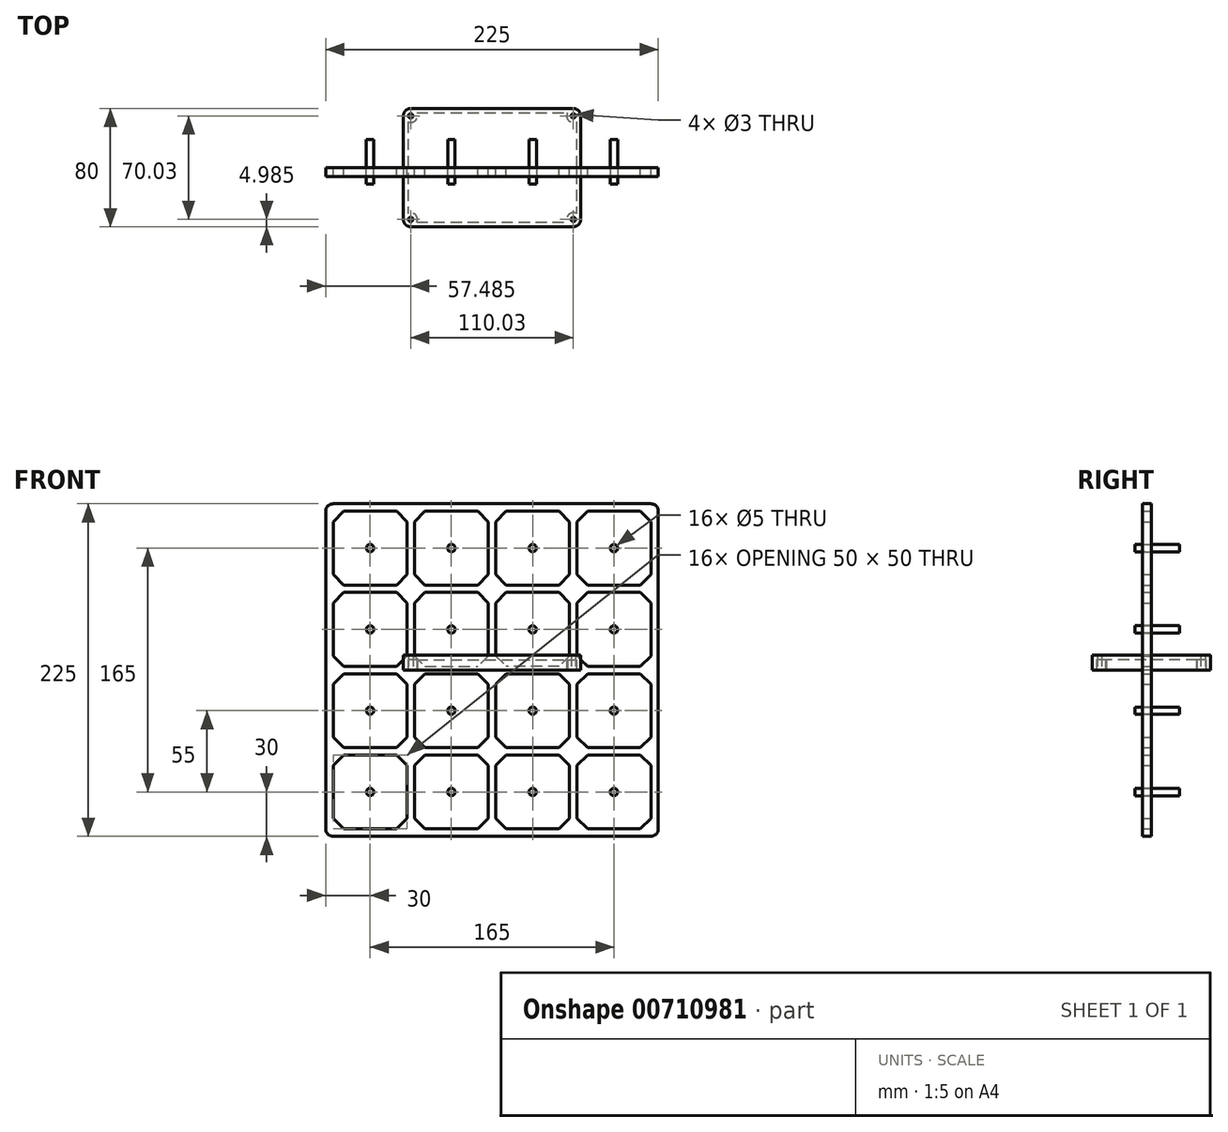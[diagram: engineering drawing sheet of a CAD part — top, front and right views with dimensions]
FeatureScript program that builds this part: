
annotation { "Feature Type Name" : "Feature", "Feature Type Description" : "" }
export const myFeature = defineFeature(function(context is Context, id is Id, definition is map)
    precondition{}
    {
        {
            var Q0;
            Q0=qCreatedBy(makeId("Front.planeOp"),FACE);
            var sketch = newSketch(context, id + "F0", { "sketchPlane" : qUnion([Q0])});
            skLineSegment(sketch, "E0.bottom", {"start": v(-112.5, 112.5) * mm, "end": v(112.5, 112.5) * mm});
            skLineSegment(sketch, "E0.top", {"start": v(-112.5, -112.5) * mm, "end": v(112.5, -112.5) * mm});
            skLineSegment(sketch, "E0.left", {"start": v(-112.5, 112.5) * mm, "end": v(-112.5, -112.5) * mm});
            skLineSegment(sketch, "E0.right", {"start": v(112.5, 112.5) * mm, "end": v(112.5, -112.5) * mm});
            skLineSegment(sketch, "E1", {"start": v(-107.5, 82.5) * mm, "end": v(-57.5, 82.5) * mm, "construction": true});
            skLineSegment(sketch, "E2", {"start": v(-82.5, 107.5) * mm, "end": v(-82.5, 57.5) * mm, "construction": true});
            skPoint(sketch, "E3", {"position": v(-82.5, 82.5) * mm});
            skLineSegment(sketch, "E4", {"start": v(-107.5, 82.5) * mm, "end": v(-107.5, 100.43) * mm});
            skLineSegment(sketch, "E5", {"start": v(-107.5, 100.43) * mm, "end": v(-100.43, 107.5) * mm});
            skLineSegment(sketch, "E6", {"start": v(-100.43, 107.5) * mm, "end": v(-82.5, 107.5) * mm});
            skLineSegment(sketch, "E7.MirrorCS", {"start": v(-57.5, 82.5) * mm, "end": v(-57.5, 100.43) * mm});
            skLineSegment(sketch, "E8.MirrorCS", {"start": v(-64.57, 107.5) * mm, "end": v(-82.5, 107.5) * mm});
            skLineSegment(sketch, "E9.MirrorCS", {"start": v(-57.5, 100.43) * mm, "end": v(-64.57, 107.5) * mm});
            skLineSegment(sketch, "E10.MirrorCS", {"start": v(-57.5, 82.5) * mm, "end": v(-107.5, 82.5) * mm, "construction": true});
            skLineSegment(sketch, "E11.MirrorCS", {"start": v(-57.5, 82.5) * mm, "end": v(-57.5, 64.57) * mm});
            skLineSegment(sketch, "E12.MirrorCS", {"start": v(-57.5, 64.57) * mm, "end": v(-64.57, 57.5) * mm});
            skLineSegment(sketch, "E13.MirrorCS", {"start": v(-64.57, 57.5) * mm, "end": v(-82.5, 57.5) * mm});
            skLineSegment(sketch, "E14.MirrorCS", {"start": v(-100.43, 57.5) * mm, "end": v(-82.5, 57.5) * mm});
            skLineSegment(sketch, "E15.MirrorCS", {"start": v(-107.5, 82.5) * mm, "end": v(-107.5, 64.57) * mm});
            skLineSegment(sketch, "E16.MirrorCS", {"start": v(-107.5, 64.57) * mm, "end": v(-100.43, 57.5) * mm});
            skLineSegment(sketch, "E17.0.1.0", {"start": v(-107.5, 45.43) * mm, "end": v(-100.43, 52.5) * mm});
            skPoint(sketch, "E17.0.1.1", {"position": v(-82.5, 27.5) * mm});
            skLineSegment(sketch, "E17.0.1.2", {"start": v(-57.5, 27.5) * mm, "end": v(-57.5, 9.57) * mm});
            skLineSegment(sketch, "E17.0.1.3", {"start": v(-57.5, 45.43) * mm, "end": v(-64.57, 52.5) * mm});
            skLineSegment(sketch, "E17.0.1.4", {"start": v(-57.5, 27.5) * mm, "end": v(-57.5, 45.43) * mm});
            skLineSegment(sketch, "E17.0.1.5", {"start": v(-57.5, 9.57) * mm, "end": v(-64.57, 2.5) * mm});
            skLineSegment(sketch, "E17.0.1.6", {"start": v(-107.5, 27.5) * mm, "end": v(-107.5, 45.43) * mm});
            skLineSegment(sketch, "E17.0.1.7", {"start": v(-64.57, 2.5) * mm, "end": v(-82.5, 2.5) * mm});
            skLineSegment(sketch, "E17.0.1.8", {"start": v(-82.5, 52.5) * mm, "end": v(-82.5, 2.5) * mm, "construction": true});
            skLineSegment(sketch, "E17.0.1.9", {"start": v(-57.5, 27.5) * mm, "end": v(-107.5, 27.5) * mm, "construction": true});
            skLineSegment(sketch, "E17.0.1.10", {"start": v(-107.5, 27.5) * mm, "end": v(-107.5, 9.57) * mm});
            skLineSegment(sketch, "E17.0.1.11", {"start": v(-107.5, 9.57) * mm, "end": v(-100.43, 2.5) * mm});
            skLineSegment(sketch, "E17.0.1.12", {"start": v(-64.57, 52.5) * mm, "end": v(-82.5, 52.5) * mm});
            skLineSegment(sketch, "E17.0.1.13", {"start": v(-100.43, 52.5) * mm, "end": v(-82.5, 52.5) * mm});
            skLineSegment(sketch, "E17.0.1.14", {"start": v(-100.43, 2.5) * mm, "end": v(-82.5, 2.5) * mm});
            skLineSegment(sketch, "E17.0.1.15", {"start": v(-107.5, 45.43) * mm, "end": v(-100.43, 52.5) * mm});
            skLineSegment(sketch, "E17.0.1.16", {"start": v(-107.5, 27.5) * mm, "end": v(-107.5, 45.43) * mm});
            skLineSegment(sketch, "E17.0.1.17", {"start": v(-57.5, 27.5) * mm, "end": v(-107.5, 27.5) * mm, "construction": true});
            skLineSegment(sketch, "E17.0.1.18", {"start": v(-57.5, 45.43) * mm, "end": v(-64.57, 52.5) * mm});
            skPoint(sketch, "E17.0.1.19", {"position": v(-82.5, 27.5) * mm});
            skLineSegment(sketch, "E17.0.1.20", {"start": v(-100.43, 52.5) * mm, "end": v(-82.5, 52.5) * mm});
            skLineSegment(sketch, "E17.0.1.21", {"start": v(-57.5, 27.5) * mm, "end": v(-57.5, 45.43) * mm});
            skLineSegment(sketch, "E17.0.1.22", {"start": v(-64.57, 52.5) * mm, "end": v(-82.5, 52.5) * mm});
            skLineSegment(sketch, "E17.0.1.23", {"start": v(-107.5, 27.5) * mm, "end": v(-57.5, 27.5) * mm, "construction": true});
            skLineSegment(sketch, "E17.0.1.24", {"start": v(-57.5, 45.43) * mm, "end": v(-64.57, 52.5) * mm});
            skLineSegment(sketch, "E17.0.1.25", {"start": v(-107.5, 45.43) * mm, "end": v(-100.43, 52.5) * mm});
            skLineSegment(sketch, "E17.0.1.26", {"start": v(-64.57, 52.5) * mm, "end": v(-82.5, 52.5) * mm});
            skLineSegment(sketch, "E17.0.1.27", {"start": v(-100.43, 52.5) * mm, "end": v(-82.5, 52.5) * mm});
            skLineSegment(sketch, "E17.0.1.28", {"start": v(-100.43, 52.5) * mm, "end": v(-82.5, 52.5) * mm});
            skLineSegment(sketch, "E17.0.1.29", {"start": v(-64.57, 52.5) * mm, "end": v(-82.5, 52.5) * mm});
            skLineSegment(sketch, "E17.0.1.30", {"start": v(-107.5, 27.5) * mm, "end": v(-57.5, 27.5) * mm, "construction": true});
            skLineSegment(sketch, "E17.0.2.0", {"start": v(-107.5, -9.57) * mm, "end": v(-100.43, -2.5) * mm});
            skPoint(sketch, "E17.0.2.1", {"position": v(-82.5, -27.5) * mm});
            skLineSegment(sketch, "E17.0.2.2", {"start": v(-57.5, -27.5) * mm, "end": v(-57.5, -45.43) * mm});
            skLineSegment(sketch, "E17.0.2.3", {"start": v(-57.5, -9.57) * mm, "end": v(-64.57, -2.5) * mm});
            skLineSegment(sketch, "E17.0.2.4", {"start": v(-57.5, -27.5) * mm, "end": v(-57.5, -9.57) * mm});
            skLineSegment(sketch, "E17.0.2.5", {"start": v(-57.5, -45.43) * mm, "end": v(-64.57, -52.5) * mm});
            skLineSegment(sketch, "E17.0.2.6", {"start": v(-107.5, -27.5) * mm, "end": v(-107.5, -9.57) * mm});
            skLineSegment(sketch, "E17.0.2.7", {"start": v(-64.57, -52.5) * mm, "end": v(-82.5, -52.5) * mm});
            skLineSegment(sketch, "E17.0.2.8", {"start": v(-82.5, -2.5) * mm, "end": v(-82.5, -52.5) * mm, "construction": true});
            skLineSegment(sketch, "E17.0.2.9", {"start": v(-57.5, -27.5) * mm, "end": v(-107.5, -27.5) * mm, "construction": true});
            skLineSegment(sketch, "E17.0.2.10", {"start": v(-107.5, -27.5) * mm, "end": v(-107.5, -45.43) * mm});
            skLineSegment(sketch, "E17.0.2.11", {"start": v(-107.5, -45.43) * mm, "end": v(-100.43, -52.5) * mm});
            skLineSegment(sketch, "E17.0.2.12", {"start": v(-64.57, -2.5) * mm, "end": v(-82.5, -2.5) * mm});
            skLineSegment(sketch, "E17.0.2.13", {"start": v(-100.43, -2.5) * mm, "end": v(-82.5, -2.5) * mm});
            skLineSegment(sketch, "E17.0.2.14", {"start": v(-100.43, -52.5) * mm, "end": v(-82.5, -52.5) * mm});
            skLineSegment(sketch, "E17.0.2.15", {"start": v(-107.5, -9.57) * mm, "end": v(-100.43, -2.5) * mm});
            skLineSegment(sketch, "E17.0.2.16", {"start": v(-107.5, -27.5) * mm, "end": v(-107.5, -9.57) * mm});
            skLineSegment(sketch, "E17.0.2.17", {"start": v(-57.5, -27.5) * mm, "end": v(-107.5, -27.5) * mm, "construction": true});
            skLineSegment(sketch, "E17.0.2.18", {"start": v(-57.5, -9.57) * mm, "end": v(-64.57, -2.5) * mm});
            skPoint(sketch, "E17.0.2.19", {"position": v(-82.5, -27.5) * mm});
            skLineSegment(sketch, "E17.0.2.20", {"start": v(-100.43, -2.5) * mm, "end": v(-82.5, -2.5) * mm});
            skLineSegment(sketch, "E17.0.2.21", {"start": v(-57.5, -27.5) * mm, "end": v(-57.5, -9.57) * mm});
            skLineSegment(sketch, "E17.0.2.22", {"start": v(-64.57, -2.5) * mm, "end": v(-82.5, -2.5) * mm});
            skLineSegment(sketch, "E17.0.2.23", {"start": v(-107.5, -27.5) * mm, "end": v(-57.5, -27.5) * mm, "construction": true});
            skLineSegment(sketch, "E17.0.2.24", {"start": v(-57.5, -9.57) * mm, "end": v(-64.57, -2.5) * mm});
            skLineSegment(sketch, "E17.0.2.25", {"start": v(-107.5, -9.57) * mm, "end": v(-100.43, -2.5) * mm});
            skLineSegment(sketch, "E17.0.2.26", {"start": v(-64.57, -2.5) * mm, "end": v(-82.5, -2.5) * mm});
            skLineSegment(sketch, "E17.0.2.27", {"start": v(-100.43, -2.5) * mm, "end": v(-82.5, -2.5) * mm});
            skLineSegment(sketch, "E17.0.2.28", {"start": v(-100.43, -2.5) * mm, "end": v(-82.5, -2.5) * mm});
            skLineSegment(sketch, "E17.0.2.29", {"start": v(-64.57, -2.5) * mm, "end": v(-82.5, -2.5) * mm});
            skLineSegment(sketch, "E17.0.2.30", {"start": v(-107.5, -27.5) * mm, "end": v(-57.5, -27.5) * mm, "construction": true});
            skLineSegment(sketch, "E17.0.3.0", {"start": v(-107.5, -64.57) * mm, "end": v(-100.43, -57.5) * mm});
            skPoint(sketch, "E17.0.3.1", {"position": v(-82.5, -82.5) * mm});
            skLineSegment(sketch, "E17.0.3.2", {"start": v(-57.5, -82.5) * mm, "end": v(-57.5, -100.43) * mm});
            skLineSegment(sketch, "E17.0.3.3", {"start": v(-57.5, -64.57) * mm, "end": v(-64.57, -57.5) * mm});
            skLineSegment(sketch, "E17.0.3.4", {"start": v(-57.5, -82.5) * mm, "end": v(-57.5, -64.57) * mm});
            skLineSegment(sketch, "E17.0.3.5", {"start": v(-57.5, -100.43) * mm, "end": v(-64.57, -107.5) * mm});
            skLineSegment(sketch, "E17.0.3.6", {"start": v(-107.5, -82.5) * mm, "end": v(-107.5, -64.57) * mm});
            skLineSegment(sketch, "E17.0.3.7", {"start": v(-64.57, -107.5) * mm, "end": v(-82.5, -107.5) * mm});
            skLineSegment(sketch, "E17.0.3.8", {"start": v(-82.5, -57.5) * mm, "end": v(-82.5, -107.5) * mm, "construction": true});
            skLineSegment(sketch, "E17.0.3.9", {"start": v(-57.5, -82.5) * mm, "end": v(-107.5, -82.5) * mm, "construction": true});
            skLineSegment(sketch, "E17.0.3.10", {"start": v(-107.5, -82.5) * mm, "end": v(-107.5, -100.43) * mm});
            skLineSegment(sketch, "E17.0.3.11", {"start": v(-107.5, -100.43) * mm, "end": v(-100.43, -107.5) * mm});
            skLineSegment(sketch, "E17.0.3.12", {"start": v(-64.57, -57.5) * mm, "end": v(-82.5, -57.5) * mm});
            skLineSegment(sketch, "E17.0.3.13", {"start": v(-100.43, -57.5) * mm, "end": v(-82.5, -57.5) * mm});
            skLineSegment(sketch, "E17.0.3.14", {"start": v(-100.43, -107.5) * mm, "end": v(-82.5, -107.5) * mm});
            skLineSegment(sketch, "E17.0.3.15", {"start": v(-107.5, -64.57) * mm, "end": v(-100.43, -57.5) * mm});
            skLineSegment(sketch, "E17.0.3.16", {"start": v(-107.5, -82.5) * mm, "end": v(-107.5, -64.57) * mm});
            skLineSegment(sketch, "E17.0.3.17", {"start": v(-57.5, -82.5) * mm, "end": v(-107.5, -82.5) * mm, "construction": true});
            skLineSegment(sketch, "E17.0.3.18", {"start": v(-57.5, -64.57) * mm, "end": v(-64.57, -57.5) * mm});
            skPoint(sketch, "E17.0.3.19", {"position": v(-82.5, -82.5) * mm});
            skLineSegment(sketch, "E17.0.3.20", {"start": v(-100.43, -57.5) * mm, "end": v(-82.5, -57.5) * mm});
            skLineSegment(sketch, "E17.0.3.21", {"start": v(-57.5, -82.5) * mm, "end": v(-57.5, -64.57) * mm});
            skLineSegment(sketch, "E17.0.3.22", {"start": v(-64.57, -57.5) * mm, "end": v(-82.5, -57.5) * mm});
            skLineSegment(sketch, "E17.0.3.23", {"start": v(-107.5, -82.5) * mm, "end": v(-57.5, -82.5) * mm, "construction": true});
            skLineSegment(sketch, "E17.0.3.24", {"start": v(-57.5, -64.57) * mm, "end": v(-64.57, -57.5) * mm});
            skLineSegment(sketch, "E17.0.3.25", {"start": v(-107.5, -64.57) * mm, "end": v(-100.43, -57.5) * mm});
            skLineSegment(sketch, "E17.0.3.26", {"start": v(-64.57, -57.5) * mm, "end": v(-82.5, -57.5) * mm});
            skLineSegment(sketch, "E17.0.3.27", {"start": v(-100.43, -57.5) * mm, "end": v(-82.5, -57.5) * mm});
            skLineSegment(sketch, "E17.0.3.28", {"start": v(-100.43, -57.5) * mm, "end": v(-82.5, -57.5) * mm});
            skLineSegment(sketch, "E17.0.3.29", {"start": v(-64.57, -57.5) * mm, "end": v(-82.5, -57.5) * mm});
            skLineSegment(sketch, "E17.0.3.30", {"start": v(-107.5, -82.5) * mm, "end": v(-57.5, -82.5) * mm, "construction": true});
            skLineSegment(sketch, "E17.1.0.0", {"start": v(-52.5, 100.43) * mm, "end": v(-45.43, 107.5) * mm});
            skPoint(sketch, "E17.1.0.1", {"position": v(-27.5, 82.5) * mm});
            skLineSegment(sketch, "E17.1.0.2", {"start": v(-2.5, 82.5) * mm, "end": v(-2.5, 64.57) * mm});
            skLineSegment(sketch, "E17.1.0.3", {"start": v(-2.5, 100.43) * mm, "end": v(-9.57, 107.5) * mm});
            skLineSegment(sketch, "E17.1.0.4", {"start": v(-2.5, 82.5) * mm, "end": v(-2.5, 100.43) * mm});
            skLineSegment(sketch, "E17.1.0.5", {"start": v(-2.5, 64.57) * mm, "end": v(-9.57, 57.5) * mm});
            skLineSegment(sketch, "E17.1.0.6", {"start": v(-52.5, 82.5) * mm, "end": v(-52.5, 100.43) * mm});
            skLineSegment(sketch, "E17.1.0.7", {"start": v(-9.57, 57.5) * mm, "end": v(-27.5, 57.5) * mm});
            skLineSegment(sketch, "E17.1.0.8", {"start": v(-27.5, 107.5) * mm, "end": v(-27.5, 57.5) * mm, "construction": true});
            skLineSegment(sketch, "E17.1.0.9", {"start": v(-2.5, 82.5) * mm, "end": v(-52.5, 82.5) * mm, "construction": true});
            skLineSegment(sketch, "E17.1.0.10", {"start": v(-52.5, 82.5) * mm, "end": v(-52.5, 64.57) * mm});
            skLineSegment(sketch, "E17.1.0.11", {"start": v(-52.5, 64.57) * mm, "end": v(-45.43, 57.5) * mm});
            skLineSegment(sketch, "E17.1.0.12", {"start": v(-9.57, 107.5) * mm, "end": v(-27.5, 107.5) * mm});
            skLineSegment(sketch, "E17.1.0.13", {"start": v(-45.43, 107.5) * mm, "end": v(-27.5, 107.5) * mm});
            skLineSegment(sketch, "E17.1.0.14", {"start": v(-45.43, 57.5) * mm, "end": v(-27.5, 57.5) * mm});
            skLineSegment(sketch, "E17.1.0.15", {"start": v(-52.5, 100.43) * mm, "end": v(-45.43, 107.5) * mm});
            skLineSegment(sketch, "E17.1.0.16", {"start": v(-52.5, 82.5) * mm, "end": v(-52.5, 100.43) * mm});
            skLineSegment(sketch, "E17.1.0.17", {"start": v(-2.5, 82.5) * mm, "end": v(-52.5, 82.5) * mm, "construction": true});
            skLineSegment(sketch, "E17.1.0.18", {"start": v(-2.5, 100.43) * mm, "end": v(-9.57, 107.5) * mm});
            skPoint(sketch, "E17.1.0.19", {"position": v(-27.5, 82.5) * mm});
            skLineSegment(sketch, "E17.1.0.20", {"start": v(-45.43, 107.5) * mm, "end": v(-27.5, 107.5) * mm});
            skLineSegment(sketch, "E17.1.0.21", {"start": v(-2.5, 82.5) * mm, "end": v(-2.5, 100.43) * mm});
            skLineSegment(sketch, "E17.1.0.22", {"start": v(-9.57, 107.5) * mm, "end": v(-27.5, 107.5) * mm});
            skLineSegment(sketch, "E17.1.0.23", {"start": v(-52.5, 82.5) * mm, "end": v(-2.5, 82.5) * mm, "construction": true});
            skLineSegment(sketch, "E17.1.0.24", {"start": v(-2.5, 100.43) * mm, "end": v(-9.57, 107.5) * mm});
            skLineSegment(sketch, "E17.1.0.25", {"start": v(-52.5, 100.43) * mm, "end": v(-45.43, 107.5) * mm});
            skLineSegment(sketch, "E17.1.0.26", {"start": v(-9.57, 107.5) * mm, "end": v(-27.5, 107.5) * mm});
            skLineSegment(sketch, "E17.1.0.27", {"start": v(-45.43, 107.5) * mm, "end": v(-27.5, 107.5) * mm});
            skLineSegment(sketch, "E17.1.0.28", {"start": v(-45.43, 107.5) * mm, "end": v(-27.5, 107.5) * mm});
            skLineSegment(sketch, "E17.1.0.29", {"start": v(-9.57, 107.5) * mm, "end": v(-27.5, 107.5) * mm});
            skLineSegment(sketch, "E17.1.0.30", {"start": v(-52.5, 82.5) * mm, "end": v(-2.5, 82.5) * mm, "construction": true});
            skLineSegment(sketch, "E17.1.1.0", {"start": v(-52.5, 45.43) * mm, "end": v(-45.43, 52.5) * mm});
            skPoint(sketch, "E17.1.1.1", {"position": v(-27.5, 27.5) * mm});
            skLineSegment(sketch, "E17.1.1.2", {"start": v(-2.5, 27.5) * mm, "end": v(-2.5, 9.57) * mm});
            skLineSegment(sketch, "E17.1.1.3", {"start": v(-2.5, 45.43) * mm, "end": v(-9.57, 52.5) * mm});
            skLineSegment(sketch, "E17.1.1.4", {"start": v(-2.5, 27.5) * mm, "end": v(-2.5, 45.43) * mm});
            skLineSegment(sketch, "E17.1.1.5", {"start": v(-2.5, 9.57) * mm, "end": v(-9.57, 2.5) * mm});
            skLineSegment(sketch, "E17.1.1.6", {"start": v(-52.5, 27.5) * mm, "end": v(-52.5, 45.43) * mm});
            skLineSegment(sketch, "E17.1.1.7", {"start": v(-9.57, 2.5) * mm, "end": v(-27.5, 2.5) * mm});
            skLineSegment(sketch, "E17.1.1.8", {"start": v(-27.5, 52.5) * mm, "end": v(-27.5, 2.5) * mm, "construction": true});
            skLineSegment(sketch, "E17.1.1.9", {"start": v(-2.5, 27.5) * mm, "end": v(-52.5, 27.5) * mm, "construction": true});
            skLineSegment(sketch, "E17.1.1.10", {"start": v(-52.5, 27.5) * mm, "end": v(-52.5, 9.57) * mm});
            skLineSegment(sketch, "E17.1.1.11", {"start": v(-52.5, 9.57) * mm, "end": v(-45.43, 2.5) * mm});
            skLineSegment(sketch, "E17.1.1.12", {"start": v(-9.57, 52.5) * mm, "end": v(-27.5, 52.5) * mm});
            skLineSegment(sketch, "E17.1.1.13", {"start": v(-45.43, 52.5) * mm, "end": v(-27.5, 52.5) * mm});
            skLineSegment(sketch, "E17.1.1.14", {"start": v(-45.43, 2.5) * mm, "end": v(-27.5, 2.5) * mm});
            skLineSegment(sketch, "E17.1.1.15", {"start": v(-52.5, 45.43) * mm, "end": v(-45.43, 52.5) * mm});
            skLineSegment(sketch, "E17.1.1.16", {"start": v(-52.5, 27.5) * mm, "end": v(-52.5, 45.43) * mm});
            skLineSegment(sketch, "E17.1.1.17", {"start": v(-2.5, 27.5) * mm, "end": v(-52.5, 27.5) * mm, "construction": true});
            skLineSegment(sketch, "E17.1.1.18", {"start": v(-2.5, 45.43) * mm, "end": v(-9.57, 52.5) * mm});
            skPoint(sketch, "E17.1.1.19", {"position": v(-27.5, 27.5) * mm});
            skLineSegment(sketch, "E17.1.1.20", {"start": v(-45.43, 52.5) * mm, "end": v(-27.5, 52.5) * mm});
            skLineSegment(sketch, "E17.1.1.21", {"start": v(-2.5, 27.5) * mm, "end": v(-2.5, 45.43) * mm});
            skLineSegment(sketch, "E17.1.1.22", {"start": v(-9.57, 52.5) * mm, "end": v(-27.5, 52.5) * mm});
            skLineSegment(sketch, "E17.1.1.23", {"start": v(-52.5, 27.5) * mm, "end": v(-2.5, 27.5) * mm, "construction": true});
            skLineSegment(sketch, "E17.1.1.24", {"start": v(-2.5, 45.43) * mm, "end": v(-9.57, 52.5) * mm});
            skLineSegment(sketch, "E17.1.1.25", {"start": v(-52.5, 45.43) * mm, "end": v(-45.43, 52.5) * mm});
            skLineSegment(sketch, "E17.1.1.26", {"start": v(-9.57, 52.5) * mm, "end": v(-27.5, 52.5) * mm});
            skLineSegment(sketch, "E17.1.1.27", {"start": v(-45.43, 52.5) * mm, "end": v(-27.5, 52.5) * mm});
            skLineSegment(sketch, "E17.1.1.28", {"start": v(-45.43, 52.5) * mm, "end": v(-27.5, 52.5) * mm});
            skLineSegment(sketch, "E17.1.1.29", {"start": v(-9.57, 52.5) * mm, "end": v(-27.5, 52.5) * mm});
            skLineSegment(sketch, "E17.1.1.30", {"start": v(-52.5, 27.5) * mm, "end": v(-2.5, 27.5) * mm, "construction": true});
            skLineSegment(sketch, "E17.1.2.0", {"start": v(-52.5, -9.57) * mm, "end": v(-45.43, -2.5) * mm});
            skPoint(sketch, "E17.1.2.1", {"position": v(-27.5, -27.5) * mm});
            skLineSegment(sketch, "E17.1.2.2", {"start": v(-2.5, -27.5) * mm, "end": v(-2.5, -45.43) * mm});
            skLineSegment(sketch, "E17.1.2.3", {"start": v(-2.5, -9.57) * mm, "end": v(-9.57, -2.5) * mm});
            skLineSegment(sketch, "E17.1.2.4", {"start": v(-2.5, -27.5) * mm, "end": v(-2.5, -9.57) * mm});
            skLineSegment(sketch, "E17.1.2.5", {"start": v(-2.5, -45.43) * mm, "end": v(-9.57, -52.5) * mm});
            skLineSegment(sketch, "E17.1.2.6", {"start": v(-52.5, -27.5) * mm, "end": v(-52.5, -9.57) * mm});
            skLineSegment(sketch, "E17.1.2.7", {"start": v(-9.57, -52.5) * mm, "end": v(-27.5, -52.5) * mm});
            skLineSegment(sketch, "E17.1.2.8", {"start": v(-27.5, -2.5) * mm, "end": v(-27.5, -52.5) * mm, "construction": true});
            skLineSegment(sketch, "E17.1.2.9", {"start": v(-2.5, -27.5) * mm, "end": v(-52.5, -27.5) * mm, "construction": true});
            skLineSegment(sketch, "E17.1.2.10", {"start": v(-52.5, -27.5) * mm, "end": v(-52.5, -45.43) * mm});
            skLineSegment(sketch, "E17.1.2.11", {"start": v(-52.5, -45.43) * mm, "end": v(-45.43, -52.5) * mm});
            skLineSegment(sketch, "E17.1.2.12", {"start": v(-9.57, -2.5) * mm, "end": v(-27.5, -2.5) * mm});
            skLineSegment(sketch, "E17.1.2.13", {"start": v(-45.43, -2.5) * mm, "end": v(-27.5, -2.5) * mm});
            skLineSegment(sketch, "E17.1.2.14", {"start": v(-45.43, -52.5) * mm, "end": v(-27.5, -52.5) * mm});
            skLineSegment(sketch, "E17.1.2.15", {"start": v(-52.5, -9.57) * mm, "end": v(-45.43, -2.5) * mm});
            skLineSegment(sketch, "E17.1.2.16", {"start": v(-52.5, -27.5) * mm, "end": v(-52.5, -9.57) * mm});
            skLineSegment(sketch, "E17.1.2.17", {"start": v(-2.5, -27.5) * mm, "end": v(-52.5, -27.5) * mm, "construction": true});
            skLineSegment(sketch, "E17.1.2.18", {"start": v(-2.5, -9.57) * mm, "end": v(-9.57, -2.5) * mm});
            skPoint(sketch, "E17.1.2.19", {"position": v(-27.5, -27.5) * mm});
            skLineSegment(sketch, "E17.1.2.20", {"start": v(-45.43, -2.5) * mm, "end": v(-27.5, -2.5) * mm});
            skLineSegment(sketch, "E17.1.2.21", {"start": v(-2.5, -27.5) * mm, "end": v(-2.5, -9.57) * mm});
            skLineSegment(sketch, "E17.1.2.22", {"start": v(-9.57, -2.5) * mm, "end": v(-27.5, -2.5) * mm});
            skLineSegment(sketch, "E17.1.2.23", {"start": v(-52.5, -27.5) * mm, "end": v(-2.5, -27.5) * mm, "construction": true});
            skLineSegment(sketch, "E17.1.2.24", {"start": v(-2.5, -9.57) * mm, "end": v(-9.57, -2.5) * mm});
            skLineSegment(sketch, "E17.1.2.25", {"start": v(-52.5, -9.57) * mm, "end": v(-45.43, -2.5) * mm});
            skLineSegment(sketch, "E17.1.2.26", {"start": v(-9.57, -2.5) * mm, "end": v(-27.5, -2.5) * mm});
            skLineSegment(sketch, "E17.1.2.27", {"start": v(-45.43, -2.5) * mm, "end": v(-27.5, -2.5) * mm});
            skLineSegment(sketch, "E17.1.2.28", {"start": v(-45.43, -2.5) * mm, "end": v(-27.5, -2.5) * mm});
            skLineSegment(sketch, "E17.1.2.29", {"start": v(-9.57, -2.5) * mm, "end": v(-27.5, -2.5) * mm});
            skLineSegment(sketch, "E17.1.2.30", {"start": v(-52.5, -27.5) * mm, "end": v(-2.5, -27.5) * mm, "construction": true});
            skLineSegment(sketch, "E17.1.3.0", {"start": v(-52.5, -64.57) * mm, "end": v(-45.43, -57.5) * mm});
            skPoint(sketch, "E17.1.3.1", {"position": v(-27.5, -82.5) * mm});
            skLineSegment(sketch, "E17.1.3.2", {"start": v(-2.5, -82.5) * mm, "end": v(-2.5, -100.43) * mm});
            skLineSegment(sketch, "E17.1.3.3", {"start": v(-2.5, -64.57) * mm, "end": v(-9.57, -57.5) * mm});
            skLineSegment(sketch, "E17.1.3.4", {"start": v(-2.5, -82.5) * mm, "end": v(-2.5, -64.57) * mm});
            skLineSegment(sketch, "E17.1.3.5", {"start": v(-2.5, -100.43) * mm, "end": v(-9.57, -107.5) * mm});
            skLineSegment(sketch, "E17.1.3.6", {"start": v(-52.5, -82.5) * mm, "end": v(-52.5, -64.57) * mm});
            skLineSegment(sketch, "E17.1.3.7", {"start": v(-9.57, -107.5) * mm, "end": v(-27.5, -107.5) * mm});
            skLineSegment(sketch, "E17.1.3.8", {"start": v(-27.5, -57.5) * mm, "end": v(-27.5, -107.5) * mm, "construction": true});
            skLineSegment(sketch, "E17.1.3.9", {"start": v(-2.5, -82.5) * mm, "end": v(-52.5, -82.5) * mm, "construction": true});
            skLineSegment(sketch, "E17.1.3.10", {"start": v(-52.5, -82.5) * mm, "end": v(-52.5, -100.43) * mm});
            skLineSegment(sketch, "E17.1.3.11", {"start": v(-52.5, -100.43) * mm, "end": v(-45.43, -107.5) * mm});
            skLineSegment(sketch, "E17.1.3.12", {"start": v(-9.57, -57.5) * mm, "end": v(-27.5, -57.5) * mm});
            skLineSegment(sketch, "E17.1.3.13", {"start": v(-45.43, -57.5) * mm, "end": v(-27.5, -57.5) * mm});
            skLineSegment(sketch, "E17.1.3.14", {"start": v(-45.43, -107.5) * mm, "end": v(-27.5, -107.5) * mm});
            skLineSegment(sketch, "E17.1.3.15", {"start": v(-52.5, -64.57) * mm, "end": v(-45.43, -57.5) * mm});
            skLineSegment(sketch, "E17.1.3.16", {"start": v(-52.5, -82.5) * mm, "end": v(-52.5, -64.57) * mm});
            skLineSegment(sketch, "E17.1.3.17", {"start": v(-2.5, -82.5) * mm, "end": v(-52.5, -82.5) * mm, "construction": true});
            skLineSegment(sketch, "E17.1.3.18", {"start": v(-2.5, -64.57) * mm, "end": v(-9.57, -57.5) * mm});
            skPoint(sketch, "E17.1.3.19", {"position": v(-27.5, -82.5) * mm});
            skLineSegment(sketch, "E17.1.3.20", {"start": v(-45.43, -57.5) * mm, "end": v(-27.5, -57.5) * mm});
            skLineSegment(sketch, "E17.1.3.21", {"start": v(-2.5, -82.5) * mm, "end": v(-2.5, -64.57) * mm});
            skLineSegment(sketch, "E17.1.3.22", {"start": v(-9.57, -57.5) * mm, "end": v(-27.5, -57.5) * mm});
            skLineSegment(sketch, "E17.1.3.23", {"start": v(-52.5, -82.5) * mm, "end": v(-2.5, -82.5) * mm, "construction": true});
            skLineSegment(sketch, "E17.1.3.24", {"start": v(-2.5, -64.57) * mm, "end": v(-9.57, -57.5) * mm});
            skLineSegment(sketch, "E17.1.3.25", {"start": v(-52.5, -64.57) * mm, "end": v(-45.43, -57.5) * mm});
            skLineSegment(sketch, "E17.1.3.26", {"start": v(-9.57, -57.5) * mm, "end": v(-27.5, -57.5) * mm});
            skLineSegment(sketch, "E17.1.3.27", {"start": v(-45.43, -57.5) * mm, "end": v(-27.5, -57.5) * mm});
            skLineSegment(sketch, "E17.1.3.28", {"start": v(-45.43, -57.5) * mm, "end": v(-27.5, -57.5) * mm});
            skLineSegment(sketch, "E17.1.3.29", {"start": v(-9.57, -57.5) * mm, "end": v(-27.5, -57.5) * mm});
            skLineSegment(sketch, "E17.1.3.30", {"start": v(-52.5, -82.5) * mm, "end": v(-2.5, -82.5) * mm, "construction": true});
            skLineSegment(sketch, "E17.2.0.0", {"start": v(2.5, 100.43) * mm, "end": v(9.57, 107.5) * mm});
            skPoint(sketch, "E17.2.0.1", {"position": v(27.5, 82.5) * mm});
            skLineSegment(sketch, "E17.2.0.2", {"start": v(52.5, 82.5) * mm, "end": v(52.5, 64.57) * mm});
            skLineSegment(sketch, "E17.2.0.3", {"start": v(52.5, 100.43) * mm, "end": v(45.43, 107.5) * mm});
            skLineSegment(sketch, "E17.2.0.4", {"start": v(52.5, 82.5) * mm, "end": v(52.5, 100.43) * mm});
            skLineSegment(sketch, "E17.2.0.5", {"start": v(52.5, 64.57) * mm, "end": v(45.43, 57.5) * mm});
            skLineSegment(sketch, "E17.2.0.6", {"start": v(2.5, 82.5) * mm, "end": v(2.5, 100.43) * mm});
            skLineSegment(sketch, "E17.2.0.7", {"start": v(45.43, 57.5) * mm, "end": v(27.5, 57.5) * mm});
            skLineSegment(sketch, "E17.2.0.8", {"start": v(27.5, 107.5) * mm, "end": v(27.5, 57.5) * mm, "construction": true});
            skLineSegment(sketch, "E17.2.0.9", {"start": v(52.5, 82.5) * mm, "end": v(2.5, 82.5) * mm, "construction": true});
            skLineSegment(sketch, "E17.2.0.10", {"start": v(2.5, 82.5) * mm, "end": v(2.5, 64.57) * mm});
            skLineSegment(sketch, "E17.2.0.11", {"start": v(2.5, 64.57) * mm, "end": v(9.57, 57.5) * mm});
            skLineSegment(sketch, "E17.2.0.12", {"start": v(45.43, 107.5) * mm, "end": v(27.5, 107.5) * mm});
            skLineSegment(sketch, "E17.2.0.13", {"start": v(9.57, 107.5) * mm, "end": v(27.5, 107.5) * mm});
            skLineSegment(sketch, "E17.2.0.14", {"start": v(9.57, 57.5) * mm, "end": v(27.5, 57.5) * mm});
            skLineSegment(sketch, "E17.2.0.15", {"start": v(2.5, 100.43) * mm, "end": v(9.57, 107.5) * mm});
            skLineSegment(sketch, "E17.2.0.16", {"start": v(2.5, 82.5) * mm, "end": v(2.5, 100.43) * mm});
            skLineSegment(sketch, "E17.2.0.17", {"start": v(52.5, 82.5) * mm, "end": v(2.5, 82.5) * mm, "construction": true});
            skLineSegment(sketch, "E17.2.0.18", {"start": v(52.5, 100.43) * mm, "end": v(45.43, 107.5) * mm});
            skPoint(sketch, "E17.2.0.19", {"position": v(27.5, 82.5) * mm});
            skLineSegment(sketch, "E17.2.0.20", {"start": v(9.57, 107.5) * mm, "end": v(27.5, 107.5) * mm});
            skLineSegment(sketch, "E17.2.0.21", {"start": v(52.5, 82.5) * mm, "end": v(52.5, 100.43) * mm});
            skLineSegment(sketch, "E17.2.0.22", {"start": v(45.43, 107.5) * mm, "end": v(27.5, 107.5) * mm});
            skLineSegment(sketch, "E17.2.0.23", {"start": v(2.5, 82.5) * mm, "end": v(52.5, 82.5) * mm, "construction": true});
            skLineSegment(sketch, "E17.2.0.24", {"start": v(52.5, 100.43) * mm, "end": v(45.43, 107.5) * mm});
            skLineSegment(sketch, "E17.2.0.25", {"start": v(2.5, 100.43) * mm, "end": v(9.57, 107.5) * mm});
            skLineSegment(sketch, "E17.2.0.26", {"start": v(45.43, 107.5) * mm, "end": v(27.5, 107.5) * mm});
            skLineSegment(sketch, "E17.2.0.27", {"start": v(9.57, 107.5) * mm, "end": v(27.5, 107.5) * mm});
            skLineSegment(sketch, "E17.2.0.28", {"start": v(9.57, 107.5) * mm, "end": v(27.5, 107.5) * mm});
            skLineSegment(sketch, "E17.2.0.29", {"start": v(45.43, 107.5) * mm, "end": v(27.5, 107.5) * mm});
            skLineSegment(sketch, "E17.2.0.30", {"start": v(2.5, 82.5) * mm, "end": v(52.5, 82.5) * mm, "construction": true});
            skLineSegment(sketch, "E17.2.1.0", {"start": v(2.5, 45.43) * mm, "end": v(9.57, 52.5) * mm});
            skPoint(sketch, "E17.2.1.1", {"position": v(27.5, 27.5) * mm});
            skLineSegment(sketch, "E17.2.1.2", {"start": v(52.5, 27.5) * mm, "end": v(52.5, 9.57) * mm});
            skLineSegment(sketch, "E17.2.1.3", {"start": v(52.5, 45.43) * mm, "end": v(45.43, 52.5) * mm});
            skLineSegment(sketch, "E17.2.1.4", {"start": v(52.5, 27.5) * mm, "end": v(52.5, 45.43) * mm});
            skLineSegment(sketch, "E17.2.1.5", {"start": v(52.5, 9.57) * mm, "end": v(45.43, 2.5) * mm});
            skLineSegment(sketch, "E17.2.1.6", {"start": v(2.5, 27.5) * mm, "end": v(2.5, 45.43) * mm});
            skLineSegment(sketch, "E17.2.1.7", {"start": v(45.43, 2.5) * mm, "end": v(27.5, 2.5) * mm});
            skLineSegment(sketch, "E17.2.1.8", {"start": v(27.5, 52.5) * mm, "end": v(27.5, 2.5) * mm, "construction": true});
            skLineSegment(sketch, "E17.2.1.9", {"start": v(52.5, 27.5) * mm, "end": v(2.5, 27.5) * mm, "construction": true});
            skLineSegment(sketch, "E17.2.1.10", {"start": v(2.5, 27.5) * mm, "end": v(2.5, 9.57) * mm});
            skLineSegment(sketch, "E17.2.1.11", {"start": v(2.5, 9.57) * mm, "end": v(9.57, 2.5) * mm});
            skLineSegment(sketch, "E17.2.1.12", {"start": v(45.43, 52.5) * mm, "end": v(27.5, 52.5) * mm});
            skLineSegment(sketch, "E17.2.1.13", {"start": v(9.57, 52.5) * mm, "end": v(27.5, 52.5) * mm});
            skLineSegment(sketch, "E17.2.1.14", {"start": v(9.57, 2.5) * mm, "end": v(27.5, 2.5) * mm});
            skLineSegment(sketch, "E17.2.1.15", {"start": v(2.5, 45.43) * mm, "end": v(9.57, 52.5) * mm});
            skLineSegment(sketch, "E17.2.1.16", {"start": v(2.5, 27.5) * mm, "end": v(2.5, 45.43) * mm});
            skLineSegment(sketch, "E17.2.1.17", {"start": v(52.5, 27.5) * mm, "end": v(2.5, 27.5) * mm, "construction": true});
            skLineSegment(sketch, "E17.2.1.18", {"start": v(52.5, 45.43) * mm, "end": v(45.43, 52.5) * mm});
            skPoint(sketch, "E17.2.1.19", {"position": v(27.5, 27.5) * mm});
            skLineSegment(sketch, "E17.2.1.20", {"start": v(9.57, 52.5) * mm, "end": v(27.5, 52.5) * mm});
            skLineSegment(sketch, "E17.2.1.21", {"start": v(52.5, 27.5) * mm, "end": v(52.5, 45.43) * mm});
            skLineSegment(sketch, "E17.2.1.22", {"start": v(45.43, 52.5) * mm, "end": v(27.5, 52.5) * mm});
            skLineSegment(sketch, "E17.2.1.23", {"start": v(2.5, 27.5) * mm, "end": v(52.5, 27.5) * mm, "construction": true});
            skLineSegment(sketch, "E17.2.1.24", {"start": v(52.5, 45.43) * mm, "end": v(45.43, 52.5) * mm});
            skLineSegment(sketch, "E17.2.1.25", {"start": v(2.5, 45.43) * mm, "end": v(9.57, 52.5) * mm});
            skLineSegment(sketch, "E17.2.1.26", {"start": v(45.43, 52.5) * mm, "end": v(27.5, 52.5) * mm});
            skLineSegment(sketch, "E17.2.1.27", {"start": v(9.57, 52.5) * mm, "end": v(27.5, 52.5) * mm});
            skLineSegment(sketch, "E17.2.1.28", {"start": v(9.57, 52.5) * mm, "end": v(27.5, 52.5) * mm});
            skLineSegment(sketch, "E17.2.1.29", {"start": v(45.43, 52.5) * mm, "end": v(27.5, 52.5) * mm});
            skLineSegment(sketch, "E17.2.1.30", {"start": v(2.5, 27.5) * mm, "end": v(52.5, 27.5) * mm, "construction": true});
            skLineSegment(sketch, "E17.2.2.0", {"start": v(2.5, -9.57) * mm, "end": v(9.57, -2.5) * mm});
            skPoint(sketch, "E17.2.2.1", {"position": v(27.5, -27.5) * mm});
            skLineSegment(sketch, "E17.2.2.2", {"start": v(52.5, -27.5) * mm, "end": v(52.5, -45.43) * mm});
            skLineSegment(sketch, "E17.2.2.3", {"start": v(52.5, -9.57) * mm, "end": v(45.43, -2.5) * mm});
            skLineSegment(sketch, "E17.2.2.4", {"start": v(52.5, -27.5) * mm, "end": v(52.5, -9.57) * mm});
            skLineSegment(sketch, "E17.2.2.5", {"start": v(52.5, -45.43) * mm, "end": v(45.43, -52.5) * mm});
            skLineSegment(sketch, "E17.2.2.6", {"start": v(2.5, -27.5) * mm, "end": v(2.5, -9.57) * mm});
            skLineSegment(sketch, "E17.2.2.7", {"start": v(45.43, -52.5) * mm, "end": v(27.5, -52.5) * mm});
            skLineSegment(sketch, "E17.2.2.8", {"start": v(27.5, -2.5) * mm, "end": v(27.5, -52.5) * mm, "construction": true});
            skLineSegment(sketch, "E17.2.2.9", {"start": v(52.5, -27.5) * mm, "end": v(2.5, -27.5) * mm, "construction": true});
            skLineSegment(sketch, "E17.2.2.10", {"start": v(2.5, -27.5) * mm, "end": v(2.5, -45.43) * mm});
            skLineSegment(sketch, "E17.2.2.11", {"start": v(2.5, -45.43) * mm, "end": v(9.57, -52.5) * mm});
            skLineSegment(sketch, "E17.2.2.12", {"start": v(45.43, -2.5) * mm, "end": v(27.5, -2.5) * mm});
            skLineSegment(sketch, "E17.2.2.13", {"start": v(9.57, -2.5) * mm, "end": v(27.5, -2.5) * mm});
            skLineSegment(sketch, "E17.2.2.14", {"start": v(9.57, -52.5) * mm, "end": v(27.5, -52.5) * mm});
            skLineSegment(sketch, "E17.2.2.15", {"start": v(2.5, -9.57) * mm, "end": v(9.57, -2.5) * mm});
            skLineSegment(sketch, "E17.2.2.16", {"start": v(2.5, -27.5) * mm, "end": v(2.5, -9.57) * mm});
            skLineSegment(sketch, "E17.2.2.17", {"start": v(52.5, -27.5) * mm, "end": v(2.5, -27.5) * mm, "construction": true});
            skLineSegment(sketch, "E17.2.2.18", {"start": v(52.5, -9.57) * mm, "end": v(45.43, -2.5) * mm});
            skPoint(sketch, "E17.2.2.19", {"position": v(27.5, -27.5) * mm});
            skLineSegment(sketch, "E17.2.2.20", {"start": v(9.57, -2.5) * mm, "end": v(27.5, -2.5) * mm});
            skLineSegment(sketch, "E17.2.2.21", {"start": v(52.5, -27.5) * mm, "end": v(52.5, -9.57) * mm});
            skLineSegment(sketch, "E17.2.2.22", {"start": v(45.43, -2.5) * mm, "end": v(27.5, -2.5) * mm});
            skLineSegment(sketch, "E17.2.2.23", {"start": v(2.5, -27.5) * mm, "end": v(52.5, -27.5) * mm, "construction": true});
            skLineSegment(sketch, "E17.2.2.24", {"start": v(52.5, -9.57) * mm, "end": v(45.43, -2.5) * mm});
            skLineSegment(sketch, "E17.2.2.25", {"start": v(2.5, -9.57) * mm, "end": v(9.57, -2.5) * mm});
            skLineSegment(sketch, "E17.2.2.26", {"start": v(45.43, -2.5) * mm, "end": v(27.5, -2.5) * mm});
            skLineSegment(sketch, "E17.2.2.27", {"start": v(9.57, -2.5) * mm, "end": v(27.5, -2.5) * mm});
            skLineSegment(sketch, "E17.2.2.28", {"start": v(9.57, -2.5) * mm, "end": v(27.5, -2.5) * mm});
            skLineSegment(sketch, "E17.2.2.29", {"start": v(45.43, -2.5) * mm, "end": v(27.5, -2.5) * mm});
            skLineSegment(sketch, "E17.2.2.30", {"start": v(2.5, -27.5) * mm, "end": v(52.5, -27.5) * mm, "construction": true});
            skLineSegment(sketch, "E17.2.3.0", {"start": v(2.5, -64.57) * mm, "end": v(9.57, -57.5) * mm});
            skPoint(sketch, "E17.2.3.1", {"position": v(27.5, -82.5) * mm});
            skLineSegment(sketch, "E17.2.3.2", {"start": v(52.5, -82.5) * mm, "end": v(52.5, -100.43) * mm});
            skLineSegment(sketch, "E17.2.3.3", {"start": v(52.5, -64.57) * mm, "end": v(45.43, -57.5) * mm});
            skLineSegment(sketch, "E17.2.3.4", {"start": v(52.5, -82.5) * mm, "end": v(52.5, -64.57) * mm});
            skLineSegment(sketch, "E17.2.3.5", {"start": v(52.5, -100.43) * mm, "end": v(45.43, -107.5) * mm});
            skLineSegment(sketch, "E17.2.3.6", {"start": v(2.5, -82.5) * mm, "end": v(2.5, -64.57) * mm});
            skLineSegment(sketch, "E17.2.3.7", {"start": v(45.43, -107.5) * mm, "end": v(27.5, -107.5) * mm});
            skLineSegment(sketch, "E17.2.3.8", {"start": v(27.5, -57.5) * mm, "end": v(27.5, -107.5) * mm, "construction": true});
            skLineSegment(sketch, "E17.2.3.9", {"start": v(52.5, -82.5) * mm, "end": v(2.5, -82.5) * mm, "construction": true});
            skLineSegment(sketch, "E17.2.3.10", {"start": v(2.5, -82.5) * mm, "end": v(2.5, -100.43) * mm});
            skLineSegment(sketch, "E17.2.3.11", {"start": v(2.5, -100.43) * mm, "end": v(9.57, -107.5) * mm});
            skLineSegment(sketch, "E17.2.3.12", {"start": v(45.43, -57.5) * mm, "end": v(27.5, -57.5) * mm});
            skLineSegment(sketch, "E17.2.3.13", {"start": v(9.57, -57.5) * mm, "end": v(27.5, -57.5) * mm});
            skLineSegment(sketch, "E17.2.3.14", {"start": v(9.57, -107.5) * mm, "end": v(27.5, -107.5) * mm});
            skLineSegment(sketch, "E17.2.3.15", {"start": v(2.5, -64.57) * mm, "end": v(9.57, -57.5) * mm});
            skLineSegment(sketch, "E17.2.3.16", {"start": v(2.5, -82.5) * mm, "end": v(2.5, -64.57) * mm});
            skLineSegment(sketch, "E17.2.3.17", {"start": v(52.5, -82.5) * mm, "end": v(2.5, -82.5) * mm, "construction": true});
            skLineSegment(sketch, "E17.2.3.18", {"start": v(52.5, -64.57) * mm, "end": v(45.43, -57.5) * mm});
            skPoint(sketch, "E17.2.3.19", {"position": v(27.5, -82.5) * mm});
            skLineSegment(sketch, "E17.2.3.20", {"start": v(9.57, -57.5) * mm, "end": v(27.5, -57.5) * mm});
            skLineSegment(sketch, "E17.2.3.21", {"start": v(52.5, -82.5) * mm, "end": v(52.5, -64.57) * mm});
            skLineSegment(sketch, "E17.2.3.22", {"start": v(45.43, -57.5) * mm, "end": v(27.5, -57.5) * mm});
            skLineSegment(sketch, "E17.2.3.23", {"start": v(2.5, -82.5) * mm, "end": v(52.5, -82.5) * mm, "construction": true});
            skLineSegment(sketch, "E17.2.3.24", {"start": v(52.5, -64.57) * mm, "end": v(45.43, -57.5) * mm});
            skLineSegment(sketch, "E17.2.3.25", {"start": v(2.5, -64.57) * mm, "end": v(9.57, -57.5) * mm});
            skLineSegment(sketch, "E17.2.3.26", {"start": v(45.43, -57.5) * mm, "end": v(27.5, -57.5) * mm});
            skLineSegment(sketch, "E17.2.3.27", {"start": v(9.57, -57.5) * mm, "end": v(27.5, -57.5) * mm});
            skLineSegment(sketch, "E17.2.3.28", {"start": v(9.57, -57.5) * mm, "end": v(27.5, -57.5) * mm});
            skLineSegment(sketch, "E17.2.3.29", {"start": v(45.43, -57.5) * mm, "end": v(27.5, -57.5) * mm});
            skLineSegment(sketch, "E17.2.3.30", {"start": v(2.5, -82.5) * mm, "end": v(52.5, -82.5) * mm, "construction": true});
            skLineSegment(sketch, "E17.3.0.0", {"start": v(57.5, 100.43) * mm, "end": v(64.57, 107.5) * mm});
            skPoint(sketch, "E17.3.0.1", {"position": v(82.5, 82.5) * mm});
            skLineSegment(sketch, "E17.3.0.2", {"start": v(107.5, 82.5) * mm, "end": v(107.5, 64.57) * mm});
            skLineSegment(sketch, "E17.3.0.3", {"start": v(107.5, 100.43) * mm, "end": v(100.43, 107.5) * mm});
            skLineSegment(sketch, "E17.3.0.4", {"start": v(107.5, 82.5) * mm, "end": v(107.5, 100.43) * mm});
            skLineSegment(sketch, "E17.3.0.5", {"start": v(107.5, 64.57) * mm, "end": v(100.43, 57.5) * mm});
            skLineSegment(sketch, "E17.3.0.6", {"start": v(57.5, 82.5) * mm, "end": v(57.5, 100.43) * mm});
            skLineSegment(sketch, "E17.3.0.7", {"start": v(100.43, 57.5) * mm, "end": v(82.5, 57.5) * mm});
            skLineSegment(sketch, "E17.3.0.8", {"start": v(82.5, 107.5) * mm, "end": v(82.5, 57.5) * mm, "construction": true});
            skLineSegment(sketch, "E17.3.0.9", {"start": v(107.5, 82.5) * mm, "end": v(57.5, 82.5) * mm, "construction": true});
            skLineSegment(sketch, "E17.3.0.10", {"start": v(57.5, 82.5) * mm, "end": v(57.5, 64.57) * mm});
            skLineSegment(sketch, "E17.3.0.11", {"start": v(57.5, 64.57) * mm, "end": v(64.57, 57.5) * mm});
            skLineSegment(sketch, "E17.3.0.12", {"start": v(100.43, 107.5) * mm, "end": v(82.5, 107.5) * mm});
            skLineSegment(sketch, "E17.3.0.13", {"start": v(64.57, 107.5) * mm, "end": v(82.5, 107.5) * mm});
            skLineSegment(sketch, "E17.3.0.14", {"start": v(64.57, 57.5) * mm, "end": v(82.5, 57.5) * mm});
            skLineSegment(sketch, "E17.3.0.15", {"start": v(57.5, 100.43) * mm, "end": v(64.57, 107.5) * mm});
            skLineSegment(sketch, "E17.3.0.16", {"start": v(57.5, 82.5) * mm, "end": v(57.5, 100.43) * mm});
            skLineSegment(sketch, "E17.3.0.17", {"start": v(107.5, 82.5) * mm, "end": v(57.5, 82.5) * mm, "construction": true});
            skLineSegment(sketch, "E17.3.0.18", {"start": v(107.5, 100.43) * mm, "end": v(100.43, 107.5) * mm});
            skPoint(sketch, "E17.3.0.19", {"position": v(82.5, 82.5) * mm});
            skLineSegment(sketch, "E17.3.0.20", {"start": v(64.57, 107.5) * mm, "end": v(82.5, 107.5) * mm});
            skLineSegment(sketch, "E17.3.0.21", {"start": v(107.5, 82.5) * mm, "end": v(107.5, 100.43) * mm});
            skLineSegment(sketch, "E17.3.0.22", {"start": v(100.43, 107.5) * mm, "end": v(82.5, 107.5) * mm});
            skLineSegment(sketch, "E17.3.0.23", {"start": v(57.5, 82.5) * mm, "end": v(107.5, 82.5) * mm, "construction": true});
            skLineSegment(sketch, "E17.3.0.24", {"start": v(107.5, 100.43) * mm, "end": v(100.43, 107.5) * mm});
            skLineSegment(sketch, "E17.3.0.25", {"start": v(57.5, 100.43) * mm, "end": v(64.57, 107.5) * mm});
            skLineSegment(sketch, "E17.3.0.26", {"start": v(100.43, 107.5) * mm, "end": v(82.5, 107.5) * mm});
            skLineSegment(sketch, "E17.3.0.27", {"start": v(64.57, 107.5) * mm, "end": v(82.5, 107.5) * mm});
            skLineSegment(sketch, "E17.3.0.28", {"start": v(64.57, 107.5) * mm, "end": v(82.5, 107.5) * mm});
            skLineSegment(sketch, "E17.3.0.29", {"start": v(100.43, 107.5) * mm, "end": v(82.5, 107.5) * mm});
            skLineSegment(sketch, "E17.3.0.30", {"start": v(57.5, 82.5) * mm, "end": v(107.5, 82.5) * mm, "construction": true});
            skLineSegment(sketch, "E17.3.1.0", {"start": v(57.5, 45.43) * mm, "end": v(64.57, 52.5) * mm});
            skPoint(sketch, "E17.3.1.1", {"position": v(82.5, 27.5) * mm});
            skLineSegment(sketch, "E17.3.1.2", {"start": v(107.5, 27.5) * mm, "end": v(107.5, 9.57) * mm});
            skLineSegment(sketch, "E17.3.1.3", {"start": v(107.5, 45.43) * mm, "end": v(100.43, 52.5) * mm});
            skLineSegment(sketch, "E17.3.1.4", {"start": v(107.5, 27.5) * mm, "end": v(107.5, 45.43) * mm});
            skLineSegment(sketch, "E17.3.1.5", {"start": v(107.5, 9.57) * mm, "end": v(100.43, 2.5) * mm});
            skLineSegment(sketch, "E17.3.1.6", {"start": v(57.5, 27.5) * mm, "end": v(57.5, 45.43) * mm});
            skLineSegment(sketch, "E17.3.1.7", {"start": v(100.43, 2.5) * mm, "end": v(82.5, 2.5) * mm});
            skLineSegment(sketch, "E17.3.1.8", {"start": v(82.5, 52.5) * mm, "end": v(82.5, 2.5) * mm, "construction": true});
            skLineSegment(sketch, "E17.3.1.9", {"start": v(107.5, 27.5) * mm, "end": v(57.5, 27.5) * mm, "construction": true});
            skLineSegment(sketch, "E17.3.1.10", {"start": v(57.5, 27.5) * mm, "end": v(57.5, 9.57) * mm});
            skLineSegment(sketch, "E17.3.1.11", {"start": v(57.5, 9.57) * mm, "end": v(64.57, 2.5) * mm});
            skLineSegment(sketch, "E17.3.1.12", {"start": v(100.43, 52.5) * mm, "end": v(82.5, 52.5) * mm});
            skLineSegment(sketch, "E17.3.1.13", {"start": v(64.57, 52.5) * mm, "end": v(82.5, 52.5) * mm});
            skLineSegment(sketch, "E17.3.1.14", {"start": v(64.57, 2.5) * mm, "end": v(82.5, 2.5) * mm});
            skLineSegment(sketch, "E17.3.1.15", {"start": v(57.5, 45.43) * mm, "end": v(64.57, 52.5) * mm});
            skLineSegment(sketch, "E17.3.1.16", {"start": v(57.5, 27.5) * mm, "end": v(57.5, 45.43) * mm});
            skLineSegment(sketch, "E17.3.1.17", {"start": v(107.5, 27.5) * mm, "end": v(57.5, 27.5) * mm, "construction": true});
            skLineSegment(sketch, "E17.3.1.18", {"start": v(107.5, 45.43) * mm, "end": v(100.43, 52.5) * mm});
            skPoint(sketch, "E17.3.1.19", {"position": v(82.5, 27.5) * mm});
            skLineSegment(sketch, "E17.3.1.20", {"start": v(64.57, 52.5) * mm, "end": v(82.5, 52.5) * mm});
            skLineSegment(sketch, "E17.3.1.21", {"start": v(107.5, 27.5) * mm, "end": v(107.5, 45.43) * mm});
            skLineSegment(sketch, "E17.3.1.22", {"start": v(100.43, 52.5) * mm, "end": v(82.5, 52.5) * mm});
            skLineSegment(sketch, "E17.3.1.23", {"start": v(57.5, 27.5) * mm, "end": v(107.5, 27.5) * mm, "construction": true});
            skLineSegment(sketch, "E17.3.1.24", {"start": v(107.5, 45.43) * mm, "end": v(100.43, 52.5) * mm});
            skLineSegment(sketch, "E17.3.1.25", {"start": v(57.5, 45.43) * mm, "end": v(64.57, 52.5) * mm});
            skLineSegment(sketch, "E17.3.1.26", {"start": v(100.43, 52.5) * mm, "end": v(82.5, 52.5) * mm});
            skLineSegment(sketch, "E17.3.1.27", {"start": v(64.57, 52.5) * mm, "end": v(82.5, 52.5) * mm});
            skLineSegment(sketch, "E17.3.1.28", {"start": v(64.57, 52.5) * mm, "end": v(82.5, 52.5) * mm});
            skLineSegment(sketch, "E17.3.1.29", {"start": v(100.43, 52.5) * mm, "end": v(82.5, 52.5) * mm});
            skLineSegment(sketch, "E17.3.1.30", {"start": v(57.5, 27.5) * mm, "end": v(107.5, 27.5) * mm, "construction": true});
            skLineSegment(sketch, "E17.3.2.0", {"start": v(57.5, -9.57) * mm, "end": v(64.57, -2.5) * mm});
            skPoint(sketch, "E17.3.2.1", {"position": v(82.5, -27.5) * mm});
            skLineSegment(sketch, "E17.3.2.2", {"start": v(107.5, -27.5) * mm, "end": v(107.5, -45.43) * mm});
            skLineSegment(sketch, "E17.3.2.3", {"start": v(107.5, -9.57) * mm, "end": v(100.43, -2.5) * mm});
            skLineSegment(sketch, "E17.3.2.4", {"start": v(107.5, -27.5) * mm, "end": v(107.5, -9.57) * mm});
            skLineSegment(sketch, "E17.3.2.5", {"start": v(107.5, -45.43) * mm, "end": v(100.43, -52.5) * mm});
            skLineSegment(sketch, "E17.3.2.6", {"start": v(57.5, -27.5) * mm, "end": v(57.5, -9.57) * mm});
            skLineSegment(sketch, "E17.3.2.7", {"start": v(100.43, -52.5) * mm, "end": v(82.5, -52.5) * mm});
            skLineSegment(sketch, "E17.3.2.8", {"start": v(82.5, -2.5) * mm, "end": v(82.5, -52.5) * mm, "construction": true});
            skLineSegment(sketch, "E17.3.2.9", {"start": v(107.5, -27.5) * mm, "end": v(57.5, -27.5) * mm, "construction": true});
            skLineSegment(sketch, "E17.3.2.10", {"start": v(57.5, -27.5) * mm, "end": v(57.5, -45.43) * mm});
            skLineSegment(sketch, "E17.3.2.11", {"start": v(57.5, -45.43) * mm, "end": v(64.57, -52.5) * mm});
            skLineSegment(sketch, "E17.3.2.12", {"start": v(100.43, -2.5) * mm, "end": v(82.5, -2.5) * mm});
            skLineSegment(sketch, "E17.3.2.13", {"start": v(64.57, -2.5) * mm, "end": v(82.5, -2.5) * mm});
            skLineSegment(sketch, "E17.3.2.14", {"start": v(64.57, -52.5) * mm, "end": v(82.5, -52.5) * mm});
            skLineSegment(sketch, "E17.3.2.15", {"start": v(57.5, -9.57) * mm, "end": v(64.57, -2.5) * mm});
            skLineSegment(sketch, "E17.3.2.16", {"start": v(57.5, -27.5) * mm, "end": v(57.5, -9.57) * mm});
            skLineSegment(sketch, "E17.3.2.17", {"start": v(107.5, -27.5) * mm, "end": v(57.5, -27.5) * mm, "construction": true});
            skLineSegment(sketch, "E17.3.2.18", {"start": v(107.5, -9.57) * mm, "end": v(100.43, -2.5) * mm});
            skPoint(sketch, "E17.3.2.19", {"position": v(82.5, -27.5) * mm});
            skLineSegment(sketch, "E17.3.2.20", {"start": v(64.57, -2.5) * mm, "end": v(82.5, -2.5) * mm});
            skLineSegment(sketch, "E17.3.2.21", {"start": v(107.5, -27.5) * mm, "end": v(107.5, -9.57) * mm});
            skLineSegment(sketch, "E17.3.2.22", {"start": v(100.43, -2.5) * mm, "end": v(82.5, -2.5) * mm});
            skLineSegment(sketch, "E17.3.2.23", {"start": v(57.5, -27.5) * mm, "end": v(107.5, -27.5) * mm, "construction": true});
            skLineSegment(sketch, "E17.3.2.24", {"start": v(107.5, -9.57) * mm, "end": v(100.43, -2.5) * mm});
            skLineSegment(sketch, "E17.3.2.25", {"start": v(57.5, -9.57) * mm, "end": v(64.57, -2.5) * mm});
            skLineSegment(sketch, "E17.3.2.26", {"start": v(100.43, -2.5) * mm, "end": v(82.5, -2.5) * mm});
            skLineSegment(sketch, "E17.3.2.27", {"start": v(64.57, -2.5) * mm, "end": v(82.5, -2.5) * mm});
            skLineSegment(sketch, "E17.3.2.28", {"start": v(64.57, -2.5) * mm, "end": v(82.5, -2.5) * mm});
            skLineSegment(sketch, "E17.3.2.29", {"start": v(100.43, -2.5) * mm, "end": v(82.5, -2.5) * mm});
            skLineSegment(sketch, "E17.3.2.30", {"start": v(57.5, -27.5) * mm, "end": v(107.5, -27.5) * mm, "construction": true});
            skLineSegment(sketch, "E17.3.3.0", {"start": v(57.5, -64.57) * mm, "end": v(64.57, -57.5) * mm});
            skPoint(sketch, "E17.3.3.1", {"position": v(82.5, -82.5) * mm});
            skLineSegment(sketch, "E17.3.3.2", {"start": v(107.5, -82.5) * mm, "end": v(107.5, -100.43) * mm});
            skLineSegment(sketch, "E17.3.3.3", {"start": v(107.5, -64.57) * mm, "end": v(100.43, -57.5) * mm});
            skLineSegment(sketch, "E17.3.3.4", {"start": v(107.5, -82.5) * mm, "end": v(107.5, -64.57) * mm});
            skLineSegment(sketch, "E17.3.3.5", {"start": v(107.5, -100.43) * mm, "end": v(100.43, -107.5) * mm});
            skLineSegment(sketch, "E17.3.3.6", {"start": v(57.5, -82.5) * mm, "end": v(57.5, -64.57) * mm});
            skLineSegment(sketch, "E17.3.3.7", {"start": v(100.43, -107.5) * mm, "end": v(82.5, -107.5) * mm});
            skLineSegment(sketch, "E17.3.3.8", {"start": v(82.5, -57.5) * mm, "end": v(82.5, -107.5) * mm, "construction": true});
            skLineSegment(sketch, "E17.3.3.9", {"start": v(107.5, -82.5) * mm, "end": v(57.5, -82.5) * mm, "construction": true});
            skLineSegment(sketch, "E17.3.3.10", {"start": v(57.5, -82.5) * mm, "end": v(57.5, -100.43) * mm});
            skLineSegment(sketch, "E17.3.3.11", {"start": v(57.5, -100.43) * mm, "end": v(64.57, -107.5) * mm});
            skLineSegment(sketch, "E17.3.3.12", {"start": v(100.43, -57.5) * mm, "end": v(82.5, -57.5) * mm});
            skLineSegment(sketch, "E17.3.3.13", {"start": v(64.57, -57.5) * mm, "end": v(82.5, -57.5) * mm});
            skLineSegment(sketch, "E17.3.3.14", {"start": v(64.57, -107.5) * mm, "end": v(82.5, -107.5) * mm});
            skLineSegment(sketch, "E17.3.3.15", {"start": v(57.5, -64.57) * mm, "end": v(64.57, -57.5) * mm});
            skLineSegment(sketch, "E17.3.3.16", {"start": v(57.5, -82.5) * mm, "end": v(57.5, -64.57) * mm});
            skLineSegment(sketch, "E17.3.3.17", {"start": v(107.5, -82.5) * mm, "end": v(57.5, -82.5) * mm, "construction": true});
            skLineSegment(sketch, "E17.3.3.18", {"start": v(107.5, -64.57) * mm, "end": v(100.43, -57.5) * mm});
            skPoint(sketch, "E17.3.3.19", {"position": v(82.5, -82.5) * mm});
            skLineSegment(sketch, "E17.3.3.20", {"start": v(64.57, -57.5) * mm, "end": v(82.5, -57.5) * mm});
            skLineSegment(sketch, "E17.3.3.21", {"start": v(107.5, -82.5) * mm, "end": v(107.5, -64.57) * mm});
            skLineSegment(sketch, "E17.3.3.22", {"start": v(100.43, -57.5) * mm, "end": v(82.5, -57.5) * mm});
            skLineSegment(sketch, "E17.3.3.23", {"start": v(57.5, -82.5) * mm, "end": v(107.5, -82.5) * mm, "construction": true});
            skLineSegment(sketch, "E17.3.3.24", {"start": v(107.5, -64.57) * mm, "end": v(100.43, -57.5) * mm});
            skLineSegment(sketch, "E17.3.3.25", {"start": v(57.5, -64.57) * mm, "end": v(64.57, -57.5) * mm});
            skLineSegment(sketch, "E17.3.3.26", {"start": v(100.43, -57.5) * mm, "end": v(82.5, -57.5) * mm});
            skLineSegment(sketch, "E17.3.3.27", {"start": v(64.57, -57.5) * mm, "end": v(82.5, -57.5) * mm});
            skLineSegment(sketch, "E17.3.3.28", {"start": v(64.57, -57.5) * mm, "end": v(82.5, -57.5) * mm});
            skLineSegment(sketch, "E17.3.3.29", {"start": v(100.43, -57.5) * mm, "end": v(82.5, -57.5) * mm});
            skLineSegment(sketch, "E17.3.3.30", {"start": v(57.5, -82.5) * mm, "end": v(107.5, -82.5) * mm, "construction": true});
            skLineSegment(sketch, "E17.direction1", {"start": v(-100.43, 57.5) * mm, "end": v(-45.43, 57.5) * mm, "construction": true});
            skLineSegment(sketch, "E17.direction2", {"start": v(-100.43, 57.5) * mm, "end": v(-100.43, 2.5) * mm, "construction": true});
            skCircle(sketch, "E18", {"center": v(-82.5, 82.5) * mm, "radius": 2.5 * mm});
            skSolve(sketch);
        }
        {
            var Q0;
            Q0=makeQuery(id+"F0.imprint","IMPRINT",FACE,{"disambiguationData":[TD([[makeQuery(id+"F0.imprint","IMPRINT",EDGE,{"derivedFrom":sQuery(id+"F0.wireOp",EDGE,"E5")}),-1.0]])]});
            var Q1;
            Q1=makeQuery(id+"F0.imprint","IMPRINT",FACE,{"disambiguationData":[TD([[makeQuery(id+"F0.imprint","IMPRINT",EDGE,{"derivedFrom":sQuery(id+"F0.wireOp",EDGE,"E17.1.0.2")}),-1.0]])]});
            var Q2;
            Q2=makeQuery(id+"F0.imprint","IMPRINT",FACE,{"disambiguationData":[TD([[makeQuery(id+"F0.imprint","IMPRINT",EDGE,{"derivedFrom":sQuery(id+"F0.wireOp",EDGE,"E17.2.0.2")}),-1.0]])]});
            var Q3;
            Q3=makeQuery(id+"F0.imprint","IMPRINT",FACE,{"disambiguationData":[TD([[makeQuery(id+"F0.imprint","IMPRINT",EDGE,{"derivedFrom":sQuery(id+"F0.wireOp",EDGE,"E17.3.0.2")}),-1.0]])]});
            var Q4;
            Q4=makeQuery(id+"F0.imprint","IMPRINT",FACE,{"disambiguationData":[TD([[makeQuery(id+"F0.imprint","IMPRINT",EDGE,{"derivedFrom":sQuery(id+"F0.wireOp",EDGE,"E17.3.1.2")}),-1.0]])]});
            var Q5;
            Q5=makeQuery(id+"F0.imprint","IMPRINT",FACE,{"disambiguationData":[TD([[makeQuery(id+"F0.imprint","IMPRINT",EDGE,{"derivedFrom":sQuery(id+"F0.wireOp",EDGE,"E17.2.1.2")}),-1.0]])]});
            var Q6;
            Q6=makeQuery(id+"F0.imprint","IMPRINT",FACE,{"disambiguationData":[TD([[makeQuery(id+"F0.imprint","IMPRINT",EDGE,{"derivedFrom":sQuery(id+"F0.wireOp",EDGE,"E17.1.1.2")}),-1.0]])]});
            var Q7;
            Q7=makeQuery(id+"F0.imprint","IMPRINT",FACE,{"disambiguationData":[TD([[makeQuery(id+"F0.imprint","IMPRINT",EDGE,{"derivedFrom":sQuery(id+"F0.wireOp",EDGE,"E17.0.1.2")}),-1.0]])]});
            var Q8;
            Q8=makeQuery(id+"F0.imprint","IMPRINT",FACE,{"disambiguationData":[TD([[makeQuery(id+"F0.imprint","IMPRINT",EDGE,{"derivedFrom":sQuery(id+"F0.wireOp",EDGE,"E17.0.2.2")}),-1.0]])]});
            var Q9;
            Q9=makeQuery(id+"F0.imprint","IMPRINT",FACE,{"disambiguationData":[TD([[makeQuery(id+"F0.imprint","IMPRINT",EDGE,{"derivedFrom":sQuery(id+"F0.wireOp",EDGE,"E17.1.2.2")}),-1.0]])]});
            var Q10;
            Q10=makeQuery(id+"F0.imprint","IMPRINT",FACE,{"disambiguationData":[TD([[makeQuery(id+"F0.imprint","IMPRINT",EDGE,{"derivedFrom":sQuery(id+"F0.wireOp",EDGE,"E17.2.2.2")}),-1.0]])]});
            var Q11;
            Q11=makeQuery(id+"F0.imprint","IMPRINT",FACE,{"disambiguationData":[TD([[makeQuery(id+"F0.imprint","IMPRINT",EDGE,{"derivedFrom":sQuery(id+"F0.wireOp",EDGE,"E17.3.2.2")}),-1.0]])]});
            var Q12;
            Q12=makeQuery(id+"F0.imprint","IMPRINT",FACE,{"disambiguationData":[TD([[makeQuery(id+"F0.imprint","IMPRINT",EDGE,{"derivedFrom":sQuery(id+"F0.wireOp",EDGE,"E17.3.3.2")}),-1.0]])]});
            var Q13;
            Q13=makeQuery(id+"F0.imprint","IMPRINT",FACE,{"disambiguationData":[TD([[makeQuery(id+"F0.imprint","IMPRINT",EDGE,{"derivedFrom":sQuery(id+"F0.wireOp",EDGE,"E17.2.3.2")}),-1.0]])]});
            var Q14;
            Q14=makeQuery(id+"F0.imprint","IMPRINT",FACE,{"disambiguationData":[TD([[makeQuery(id+"F0.imprint","IMPRINT",EDGE,{"derivedFrom":sQuery(id+"F0.wireOp",EDGE,"E17.1.3.2")}),-1.0]])]});
            var Q15;
            Q15=makeQuery(id+"F0.imprint","IMPRINT",FACE,{"disambiguationData":[TD([[makeQuery(id+"F0.imprint","IMPRINT",EDGE,{"derivedFrom":sQuery(id+"F0.wireOp",EDGE,"E17.0.3.2")}),-1.0]])]});
            extrude(context, id + "F1", {"entities" : qUnion([Q0, Q1, Q2, Q3, Q4, Q5, Q6, Q7, Q8, Q9, Q10, Q11, Q12, Q13, Q14, Q15]), "depth" : 6 * mm, "offsetDistance" : 25 * mm});
        }
        {
            var Q0;
            Q0=makeQuery(id+"F0.imprint","IMPRINT",FACE,{"disambiguationData":[TD([[makeQuery(id+"F0.imprint","IMPRINT",EDGE,{"derivedFrom":sQuery(id+"F0.wireOp",EDGE,"E0.bottom")}),-1.0]])]});
            extrude(context, id + "F2", {"entities" : qUnion([Q0]), "depth" : 6 * mm, "offsetDistance" : 25 * mm});
        }
        {
            var Q0;
            Q0=makeQuery(id+"F2.opExtrude","SWEPT_EDGE",EDGE,{"disambiguationData":[OSD([sQuery(id+"F0.wireOp",EDGE,"E0.bottom"),sQuery(id+"F0.wireOp",EDGE,"E0.left")])]});
            var Q1;
            Q1=makeQuery(id+"F2.opExtrude","SWEPT_EDGE",EDGE,{"disambiguationData":[OSD([sQuery(id+"F0.wireOp",EDGE,"E0.bottom"),sQuery(id+"F0.wireOp",EDGE,"E0.right")])]});
            var Q2;
            Q2=makeQuery(id+"F2.opExtrude","SWEPT_EDGE",EDGE,{"disambiguationData":[OSD([sQuery(id+"F0.wireOp",EDGE,"E0.top"),sQuery(id+"F0.wireOp",EDGE,"E0.right")])]});
            var Q3;
            Q3=makeQuery(id+"F2.opExtrude","SWEPT_EDGE",EDGE,{"disambiguationData":[OSD([sQuery(id+"F0.wireOp",EDGE,"E0.top"),sQuery(id+"F0.wireOp",EDGE,"E0.left")])]});
            fillet(context, id + "F3", {"entities" : qUnion([Q0, Q1, Q2, Q3]), "radius" : 5 * mm, "tangentPropagation" : true, "allowEdgeOverflow" : false});
        }
        {
            var Q0;
            Q0=sQuery(id+"F0.wireOp",VERTEX,"E3");
            var Q1;
            Q1=sQuery(id+"F0.wireOp",VERTEX,"E17.1.0.1");
            var Q2;
            Q2=sQuery(id+"F0.wireOp",VERTEX,"E17.2.0.1");
            var Q3;
            Q3=sQuery(id+"F0.wireOp",VERTEX,"E17.3.0.1");
            var Q4;
            Q4=sQuery(id+"F0.wireOp",VERTEX,"E17.0.1.1");
            var Q5;
            Q5=sQuery(id+"F0.wireOp",VERTEX,"E17.1.1.1");
            var Q6;
            Q6=sQuery(id+"F0.wireOp",VERTEX,"E17.2.1.1");
            var Q7;
            Q7=sQuery(id+"F0.wireOp",VERTEX,"E17.3.1.1");
            var Q8;
            Q8=sQuery(id+"F0.wireOp",VERTEX,"E17.0.2.1");
            var Q9;
            Q9=sQuery(id+"F0.wireOp",VERTEX,"E17.1.2.1");
            var Q10;
            Q10=sQuery(id+"F0.wireOp",VERTEX,"E17.2.2.1");
            var Q11;
            Q11=sQuery(id+"F0.wireOp",VERTEX,"E17.3.2.1");
            var Q12;
            Q12=sQuery(id+"F0.wireOp",VERTEX,"E17.0.3.1");
            var Q13;
            Q13=sQuery(id+"F0.wireOp",VERTEX,"E17.1.3.1");
            var Q14;
            Q14=sQuery(id+"F0.wireOp",VERTEX,"E17.2.3.1");
            var Q15;
            Q15=sQuery(id+"F0.wireOp",VERTEX,"E17.3.3.1");
            var Q16;
            Q16=makeQuery(id+"F1.opExtrude","SWEPT_BODY",BODY,{"disambiguationData":[OSD([sQuery(id+"F0.wireOp",EDGE,"E5"),sQuery(id+"F0.wireOp",EDGE,"E6"),sQuery(id+"F0.wireOp",EDGE,"E9.MirrorCS"),sQuery(id+"F0.wireOp",EDGE,"E4"),sQuery(id+"F0.wireOp",EDGE,"E8.MirrorCS"),sQuery(id+"F0.wireOp",EDGE,"E7.MirrorCS"),sQuery(id+"F0.wireOp",EDGE,"E11.MirrorCS"),sQuery(id+"F0.wireOp",EDGE,"E12.MirrorCS"),sQuery(id+"F0.wireOp",EDGE,"E13.MirrorCS"),sQuery(id+"F0.wireOp",EDGE,"E14.MirrorCS"),sQuery(id+"F0.wireOp",EDGE,"E15.MirrorCS"),sQuery(id+"F0.wireOp",EDGE,"E16.MirrorCS")])]});
            var Q17;
            Q17=makeQuery(id+"F1.opExtrude","SWEPT_BODY",BODY,{"disambiguationData":[OSD([sQuery(id+"F0.wireOp",EDGE,"E17.0.1.2"),sQuery(id+"F0.wireOp",EDGE,"E17.0.1.5"),sQuery(id+"F0.wireOp",EDGE,"E17.0.1.7"),sQuery(id+"F0.wireOp",EDGE,"E17.0.1.10"),sQuery(id+"F0.wireOp",EDGE,"E17.0.1.11"),sQuery(id+"F0.wireOp",EDGE,"E17.0.1.14"),sQuery(id+"F0.wireOp",EDGE,"E17.0.1.16"),sQuery(id+"F0.wireOp",EDGE,"E17.0.1.21"),sQuery(id+"F0.wireOp",EDGE,"E17.0.1.24"),sQuery(id+"F0.wireOp",EDGE,"E17.0.1.25"),sQuery(id+"F0.wireOp",EDGE,"E17.0.1.28"),sQuery(id+"F0.wireOp",EDGE,"E17.0.1.29")])]});
            var Q18;
            Q18=makeQuery(id+"F1.opExtrude","SWEPT_BODY",BODY,{"disambiguationData":[OSD([sQuery(id+"F0.wireOp",EDGE,"E17.0.2.2"),sQuery(id+"F0.wireOp",EDGE,"E17.0.2.5"),sQuery(id+"F0.wireOp",EDGE,"E17.0.2.7"),sQuery(id+"F0.wireOp",EDGE,"E17.0.2.10"),sQuery(id+"F0.wireOp",EDGE,"E17.0.2.11"),sQuery(id+"F0.wireOp",EDGE,"E17.0.2.14"),sQuery(id+"F0.wireOp",EDGE,"E17.0.2.16"),sQuery(id+"F0.wireOp",EDGE,"E17.0.2.21"),sQuery(id+"F0.wireOp",EDGE,"E17.0.2.24"),sQuery(id+"F0.wireOp",EDGE,"E17.0.2.25"),sQuery(id+"F0.wireOp",EDGE,"E17.0.2.28"),sQuery(id+"F0.wireOp",EDGE,"E17.0.2.29")])]});
            var Q19;
            Q19=makeQuery(id+"F1.opExtrude","SWEPT_BODY",BODY,{"disambiguationData":[OSD([sQuery(id+"F0.wireOp",EDGE,"E17.0.3.2"),sQuery(id+"F0.wireOp",EDGE,"E17.0.3.5"),sQuery(id+"F0.wireOp",EDGE,"E17.0.3.7"),sQuery(id+"F0.wireOp",EDGE,"E17.0.3.10"),sQuery(id+"F0.wireOp",EDGE,"E17.0.3.11"),sQuery(id+"F0.wireOp",EDGE,"E17.0.3.14"),sQuery(id+"F0.wireOp",EDGE,"E17.0.3.16"),sQuery(id+"F0.wireOp",EDGE,"E17.0.3.21"),sQuery(id+"F0.wireOp",EDGE,"E17.0.3.24"),sQuery(id+"F0.wireOp",EDGE,"E17.0.3.25"),sQuery(id+"F0.wireOp",EDGE,"E17.0.3.28"),sQuery(id+"F0.wireOp",EDGE,"E17.0.3.29")])]});
            var Q20;
            Q20=makeQuery(id+"F1.opExtrude","SWEPT_BODY",BODY,{"disambiguationData":[OSD([sQuery(id+"F0.wireOp",EDGE,"E17.1.0.2"),sQuery(id+"F0.wireOp",EDGE,"E17.1.0.5"),sQuery(id+"F0.wireOp",EDGE,"E17.1.0.7"),sQuery(id+"F0.wireOp",EDGE,"E17.1.0.10"),sQuery(id+"F0.wireOp",EDGE,"E17.1.0.11"),sQuery(id+"F0.wireOp",EDGE,"E17.1.0.14"),sQuery(id+"F0.wireOp",EDGE,"E17.1.0.16"),sQuery(id+"F0.wireOp",EDGE,"E17.1.0.21"),sQuery(id+"F0.wireOp",EDGE,"E17.1.0.24"),sQuery(id+"F0.wireOp",EDGE,"E17.1.0.25"),sQuery(id+"F0.wireOp",EDGE,"E17.1.0.28"),sQuery(id+"F0.wireOp",EDGE,"E17.1.0.29")])]});
            var Q21;
            Q21=makeQuery(id+"F1.opExtrude","SWEPT_BODY",BODY,{"disambiguationData":[OSD([sQuery(id+"F0.wireOp",EDGE,"E17.1.1.2"),sQuery(id+"F0.wireOp",EDGE,"E17.1.1.5"),sQuery(id+"F0.wireOp",EDGE,"E17.1.1.7"),sQuery(id+"F0.wireOp",EDGE,"E17.1.1.10"),sQuery(id+"F0.wireOp",EDGE,"E17.1.1.11"),sQuery(id+"F0.wireOp",EDGE,"E17.1.1.14"),sQuery(id+"F0.wireOp",EDGE,"E17.1.1.16"),sQuery(id+"F0.wireOp",EDGE,"E17.1.1.21"),sQuery(id+"F0.wireOp",EDGE,"E17.1.1.24"),sQuery(id+"F0.wireOp",EDGE,"E17.1.1.25"),sQuery(id+"F0.wireOp",EDGE,"E17.1.1.28"),sQuery(id+"F0.wireOp",EDGE,"E17.1.1.29")])]});
            var Q22;
            Q22=makeQuery(id+"F1.opExtrude","SWEPT_BODY",BODY,{"disambiguationData":[OSD([sQuery(id+"F0.wireOp",EDGE,"E17.1.2.2"),sQuery(id+"F0.wireOp",EDGE,"E17.1.2.5"),sQuery(id+"F0.wireOp",EDGE,"E17.1.2.7"),sQuery(id+"F0.wireOp",EDGE,"E17.1.2.10"),sQuery(id+"F0.wireOp",EDGE,"E17.1.2.11"),sQuery(id+"F0.wireOp",EDGE,"E17.1.2.14"),sQuery(id+"F0.wireOp",EDGE,"E17.1.2.16"),sQuery(id+"F0.wireOp",EDGE,"E17.1.2.21"),sQuery(id+"F0.wireOp",EDGE,"E17.1.2.24"),sQuery(id+"F0.wireOp",EDGE,"E17.1.2.25"),sQuery(id+"F0.wireOp",EDGE,"E17.1.2.28"),sQuery(id+"F0.wireOp",EDGE,"E17.1.2.29")])]});
            var Q23;
            Q23=makeQuery(id+"F1.opExtrude","SWEPT_BODY",BODY,{"disambiguationData":[OSD([sQuery(id+"F0.wireOp",EDGE,"E17.1.3.2"),sQuery(id+"F0.wireOp",EDGE,"E17.1.3.5"),sQuery(id+"F0.wireOp",EDGE,"E17.1.3.7"),sQuery(id+"F0.wireOp",EDGE,"E17.1.3.10"),sQuery(id+"F0.wireOp",EDGE,"E17.1.3.11"),sQuery(id+"F0.wireOp",EDGE,"E17.1.3.14"),sQuery(id+"F0.wireOp",EDGE,"E17.1.3.16"),sQuery(id+"F0.wireOp",EDGE,"E17.1.3.21"),sQuery(id+"F0.wireOp",EDGE,"E17.1.3.24"),sQuery(id+"F0.wireOp",EDGE,"E17.1.3.25"),sQuery(id+"F0.wireOp",EDGE,"E17.1.3.28"),sQuery(id+"F0.wireOp",EDGE,"E17.1.3.29")])]});
            var Q24;
            Q24=makeQuery(id+"F1.opExtrude","SWEPT_BODY",BODY,{"disambiguationData":[OSD([sQuery(id+"F0.wireOp",EDGE,"E17.2.0.2"),sQuery(id+"F0.wireOp",EDGE,"E17.2.0.5"),sQuery(id+"F0.wireOp",EDGE,"E17.2.0.7"),sQuery(id+"F0.wireOp",EDGE,"E17.2.0.10"),sQuery(id+"F0.wireOp",EDGE,"E17.2.0.11"),sQuery(id+"F0.wireOp",EDGE,"E17.2.0.14"),sQuery(id+"F0.wireOp",EDGE,"E17.2.0.16"),sQuery(id+"F0.wireOp",EDGE,"E17.2.0.21"),sQuery(id+"F0.wireOp",EDGE,"E17.2.0.24"),sQuery(id+"F0.wireOp",EDGE,"E17.2.0.25"),sQuery(id+"F0.wireOp",EDGE,"E17.2.0.28"),sQuery(id+"F0.wireOp",EDGE,"E17.2.0.29")])]});
            var Q25;
            Q25=makeQuery(id+"F1.opExtrude","SWEPT_BODY",BODY,{"disambiguationData":[OSD([sQuery(id+"F0.wireOp",EDGE,"E17.2.1.2"),sQuery(id+"F0.wireOp",EDGE,"E17.2.1.5"),sQuery(id+"F0.wireOp",EDGE,"E17.2.1.7"),sQuery(id+"F0.wireOp",EDGE,"E17.2.1.10"),sQuery(id+"F0.wireOp",EDGE,"E17.2.1.11"),sQuery(id+"F0.wireOp",EDGE,"E17.2.1.14"),sQuery(id+"F0.wireOp",EDGE,"E17.2.1.16"),sQuery(id+"F0.wireOp",EDGE,"E17.2.1.21"),sQuery(id+"F0.wireOp",EDGE,"E17.2.1.24"),sQuery(id+"F0.wireOp",EDGE,"E17.2.1.25"),sQuery(id+"F0.wireOp",EDGE,"E17.2.1.28"),sQuery(id+"F0.wireOp",EDGE,"E17.2.1.29")])]});
            var Q26;
            Q26=makeQuery(id+"F1.opExtrude","SWEPT_BODY",BODY,{"disambiguationData":[OSD([sQuery(id+"F0.wireOp",EDGE,"E17.2.2.2"),sQuery(id+"F0.wireOp",EDGE,"E17.2.2.5"),sQuery(id+"F0.wireOp",EDGE,"E17.2.2.7"),sQuery(id+"F0.wireOp",EDGE,"E17.2.2.10"),sQuery(id+"F0.wireOp",EDGE,"E17.2.2.11"),sQuery(id+"F0.wireOp",EDGE,"E17.2.2.14"),sQuery(id+"F0.wireOp",EDGE,"E17.2.2.16"),sQuery(id+"F0.wireOp",EDGE,"E17.2.2.21"),sQuery(id+"F0.wireOp",EDGE,"E17.2.2.24"),sQuery(id+"F0.wireOp",EDGE,"E17.2.2.25"),sQuery(id+"F0.wireOp",EDGE,"E17.2.2.28"),sQuery(id+"F0.wireOp",EDGE,"E17.2.2.29")])]});
            var Q27;
            Q27=makeQuery(id+"F1.opExtrude","SWEPT_BODY",BODY,{"disambiguationData":[OSD([sQuery(id+"F0.wireOp",EDGE,"E17.2.3.2"),sQuery(id+"F0.wireOp",EDGE,"E17.2.3.5"),sQuery(id+"F0.wireOp",EDGE,"E17.2.3.7"),sQuery(id+"F0.wireOp",EDGE,"E17.2.3.10"),sQuery(id+"F0.wireOp",EDGE,"E17.2.3.11"),sQuery(id+"F0.wireOp",EDGE,"E17.2.3.14"),sQuery(id+"F0.wireOp",EDGE,"E17.2.3.16"),sQuery(id+"F0.wireOp",EDGE,"E17.2.3.21"),sQuery(id+"F0.wireOp",EDGE,"E17.2.3.24"),sQuery(id+"F0.wireOp",EDGE,"E17.2.3.25"),sQuery(id+"F0.wireOp",EDGE,"E17.2.3.28"),sQuery(id+"F0.wireOp",EDGE,"E17.2.3.29")])]});
            var Q28;
            Q28=makeQuery(id+"F1.opExtrude","SWEPT_BODY",BODY,{"disambiguationData":[OSD([sQuery(id+"F0.wireOp",EDGE,"E17.3.0.2"),sQuery(id+"F0.wireOp",EDGE,"E17.3.0.5"),sQuery(id+"F0.wireOp",EDGE,"E17.3.0.7"),sQuery(id+"F0.wireOp",EDGE,"E17.3.0.10"),sQuery(id+"F0.wireOp",EDGE,"E17.3.0.11"),sQuery(id+"F0.wireOp",EDGE,"E17.3.0.14"),sQuery(id+"F0.wireOp",EDGE,"E17.3.0.16"),sQuery(id+"F0.wireOp",EDGE,"E17.3.0.21"),sQuery(id+"F0.wireOp",EDGE,"E17.3.0.24"),sQuery(id+"F0.wireOp",EDGE,"E17.3.0.25"),sQuery(id+"F0.wireOp",EDGE,"E17.3.0.28"),sQuery(id+"F0.wireOp",EDGE,"E17.3.0.29")])]});
            var Q29;
            Q29=makeQuery(id+"F1.opExtrude","SWEPT_BODY",BODY,{"disambiguationData":[OSD([sQuery(id+"F0.wireOp",EDGE,"E17.3.1.2"),sQuery(id+"F0.wireOp",EDGE,"E17.3.1.5"),sQuery(id+"F0.wireOp",EDGE,"E17.3.1.7"),sQuery(id+"F0.wireOp",EDGE,"E17.3.1.10"),sQuery(id+"F0.wireOp",EDGE,"E17.3.1.11"),sQuery(id+"F0.wireOp",EDGE,"E17.3.1.14"),sQuery(id+"F0.wireOp",EDGE,"E17.3.1.16"),sQuery(id+"F0.wireOp",EDGE,"E17.3.1.21"),sQuery(id+"F0.wireOp",EDGE,"E17.3.1.24"),sQuery(id+"F0.wireOp",EDGE,"E17.3.1.25"),sQuery(id+"F0.wireOp",EDGE,"E17.3.1.28"),sQuery(id+"F0.wireOp",EDGE,"E17.3.1.29")])]});
            var Q30;
            Q30=makeQuery(id+"F1.opExtrude","SWEPT_BODY",BODY,{"disambiguationData":[OSD([sQuery(id+"F0.wireOp",EDGE,"E17.3.2.2"),sQuery(id+"F0.wireOp",EDGE,"E17.3.2.5"),sQuery(id+"F0.wireOp",EDGE,"E17.3.2.7"),sQuery(id+"F0.wireOp",EDGE,"E17.3.2.10"),sQuery(id+"F0.wireOp",EDGE,"E17.3.2.11"),sQuery(id+"F0.wireOp",EDGE,"E17.3.2.14"),sQuery(id+"F0.wireOp",EDGE,"E17.3.2.16"),sQuery(id+"F0.wireOp",EDGE,"E17.3.2.21"),sQuery(id+"F0.wireOp",EDGE,"E17.3.2.24"),sQuery(id+"F0.wireOp",EDGE,"E17.3.2.25"),sQuery(id+"F0.wireOp",EDGE,"E17.3.2.28"),sQuery(id+"F0.wireOp",EDGE,"E17.3.2.29")])]});
            var Q31;
            Q31=makeQuery(id+"F1.opExtrude","SWEPT_BODY",BODY,{"disambiguationData":[OSD([sQuery(id+"F0.wireOp",EDGE,"E17.3.3.2"),sQuery(id+"F0.wireOp",EDGE,"E17.3.3.5"),sQuery(id+"F0.wireOp",EDGE,"E17.3.3.7"),sQuery(id+"F0.wireOp",EDGE,"E17.3.3.10"),sQuery(id+"F0.wireOp",EDGE,"E17.3.3.11"),sQuery(id+"F0.wireOp",EDGE,"E17.3.3.14"),sQuery(id+"F0.wireOp",EDGE,"E17.3.3.16"),sQuery(id+"F0.wireOp",EDGE,"E17.3.3.21"),sQuery(id+"F0.wireOp",EDGE,"E17.3.3.24"),sQuery(id+"F0.wireOp",EDGE,"E17.3.3.25"),sQuery(id+"F0.wireOp",EDGE,"E17.3.3.28"),sQuery(id+"F0.wireOp",EDGE,"E17.3.3.29")])]});
            hole(context, id + "F4", {"style" : HoleStyle.SIMPLE, "endStyle" : HoleEndStyle.THROUGH, "oppositeDirection" : true, "holeDiameter" : 5 * mm, "majorDiameter" : 5 * mm, "isTappedThrough" : true, "tappedDepth" : 12 * mm, "tapClearance" : 3, "locations" : qUnion([Q0, Q1, Q2, Q3, Q4, Q5, Q6, Q7, Q8, Q9, Q10, Q11, Q12, Q13, Q14, Q15]), "scope" : qUnion([Q16, Q17, Q18, Q19, Q20, Q21, Q22, Q23, Q24, Q25, Q26, Q27, Q28, Q29, Q30, Q31])});
        }
        {
            var Q0;
            Q0=makeQuery(id+"F1.opExtrude","CAP_FACE",FACE,{"disambiguationData":[OSD([sQuery(id+"F0.wireOp",EDGE,"E5"),sQuery(id+"F0.wireOp",EDGE,"E6"),sQuery(id+"F0.wireOp",EDGE,"E9.MirrorCS"),sQuery(id+"F0.wireOp",EDGE,"E4"),sQuery(id+"F0.wireOp",EDGE,"E8.MirrorCS"),sQuery(id+"F0.wireOp",EDGE,"E7.MirrorCS"),sQuery(id+"F0.wireOp",EDGE,"E11.MirrorCS"),sQuery(id+"F0.wireOp",EDGE,"E12.MirrorCS"),sQuery(id+"F0.wireOp",EDGE,"E13.MirrorCS"),sQuery(id+"F0.wireOp",EDGE,"E14.MirrorCS"),sQuery(id+"F0.wireOp",EDGE,"E15.MirrorCS"),sQuery(id+"F0.wireOp",EDGE,"E16.MirrorCS")])],"isStart":false});
            var sketch = newSketch(context, id + "F5", { "sketchPlane" : qUnion([Q0])});
            skCircle(sketch, "E19", {"center": v(-82.5, 82.5) * mm, "radius": 2.5 * mm});
            skCircle(sketch, "E20.0.1.0", {"center": v(-82.5, 27.5) * mm, "radius": 2.5 * mm});
            skCircle(sketch, "E20.0.2.0", {"center": v(-82.5, -27.5) * mm, "radius": 2.5 * mm});
            skCircle(sketch, "E20.0.3.0", {"center": v(-82.5, -82.5) * mm, "radius": 2.5 * mm});
            skCircle(sketch, "E20.1.0.0", {"center": v(-27.5, 82.5) * mm, "radius": 2.5 * mm});
            skCircle(sketch, "E20.1.1.0", {"center": v(-27.5, 27.5) * mm, "radius": 2.5 * mm});
            skCircle(sketch, "E20.1.2.0", {"center": v(-27.5, -27.5) * mm, "radius": 2.5 * mm});
            skCircle(sketch, "E20.1.3.0", {"center": v(-27.5, -82.5) * mm, "radius": 2.5 * mm});
            skCircle(sketch, "E20.2.0.0", {"center": v(27.5, 82.5) * mm, "radius": 2.5 * mm});
            skCircle(sketch, "E20.2.1.0", {"center": v(27.5, 27.5) * mm, "radius": 2.5 * mm});
            skCircle(sketch, "E20.2.2.0", {"center": v(27.5, -27.5) * mm, "radius": 2.5 * mm});
            skCircle(sketch, "E20.2.3.0", {"center": v(27.5, -82.5) * mm, "radius": 2.5 * mm});
            skCircle(sketch, "E20.3.0.0", {"center": v(82.5, 82.5) * mm, "radius": 2.5 * mm});
            skCircle(sketch, "E20.3.1.0", {"center": v(82.5, 27.5) * mm, "radius": 2.5 * mm});
            skCircle(sketch, "E20.3.2.0", {"center": v(82.5, -27.5) * mm, "radius": 2.5 * mm});
            skCircle(sketch, "E20.3.3.0", {"center": v(82.5, -82.5) * mm, "radius": 2.5 * mm});
            skLineSegment(sketch, "E20.direction1", {"start": v(-82.5, 82.5) * mm, "end": v(-27.5, 82.5) * mm, "construction": true});
            skLineSegment(sketch, "E20.direction2", {"start": v(-82.5, 82.5) * mm, "end": v(-82.5, 27.5) * mm, "construction": true});
            skSolve(sketch);
        }
        {
            var Q0;
            Q0 = qSketchRegion(id + "F5", true);
            extrude(context, id + "F6", {"entities" : qUnion([Q0]), "oppositeDirection" : true, "depth" : 25 * mm, "offsetDistance" : 25 * mm, "hasSecondDirection" : true, "secondDirectionOppositeDirection" : false, "secondDirectionDepth" : 5 * mm});
        }
        {
            var Q0;
            Q0=qCreatedBy(makeId("Top.planeOp"),FACE);
            var sketch = newSketch(context, id + "F7", { "sketchPlane" : qUnion([Q0])});
            skLineSegment(sketch, "E21.bottom", {"start": v(-55, 40) * mm, "end": v(55, 40) * mm});
            skLineSegment(sketch, "E21.top", {"start": v(-55, -40) * mm, "end": v(55, -40) * mm});
            skLineSegment(sketch, "E21.left", {"start": v(-60, 35) * mm, "end": v(-60, -35) * mm});
            skLineSegment(sketch, "E21.right", {"start": v(60, 35) * mm, "end": v(60, -35) * mm});
            skPoint(sketch, "E22.visualSharp", {"position": v(-60, 40) * mm});
            skArc(sketch, "E22.filletArc", {"start": v(-55, 40) * mm, "mid": v(-58.54, 38.54) * mm, "end": v(-60, 35) * mm});
            skPoint(sketch, "E23.visualSharp", {"position": v(60, 40) * mm});
            skArc(sketch, "E23.filletArc", {"start": v(60, 35) * mm, "mid": v(58.54, 38.54) * mm, "end": v(55, 40) * mm});
            skPoint(sketch, "E24.visualSharp", {"position": v(60, -40) * mm});
            skArc(sketch, "E24.filletArc", {"start": v(55, -40) * mm, "mid": v(58.54, -38.54) * mm, "end": v(60, -35) * mm});
            skPoint(sketch, "E25.visualSharp", {"position": v(-60, -40) * mm});
            skArc(sketch, "E25.filletArc", {"start": v(-60, -35) * mm, "mid": v(-58.54, -38.54) * mm, "end": v(-55, -40) * mm});
            skSolve(sketch);
        }
        {
            var Q0;
            Q0=makeQuery(id+"F7.imprint","IMPRINT",FACE,{"disambiguationData":[TD([[makeQuery(id+"F7.imprint","IMPRINT",EDGE,{"derivedFrom":sQuery(id+"F7.wireOp",EDGE,"E21.bottom")}),-1.0]])]});
            extrude(context, id + "F8", {"entities" : qUnion([Q0]), "depth" : 10 * mm, "offsetDistance" : 25 * mm});
        }
        {
            var Q0;
            Q0=sQuery(id+"F7.wireOp",VERTEX,"E22.filletArc.center");
            var Q1;
            Q1=sQuery(id+"F7.wireOp",VERTEX,"E23.filletArc.center");
            var Q2;
            Q2=sQuery(id+"F7.wireOp",VERTEX,"E24.filletArc.center");
            var Q3;
            Q3=sQuery(id+"F7.wireOp",VERTEX,"E25.filletArc.center");
            var Q4;
            Q4=makeQuery(id+"F8.opExtrude","SWEPT_BODY",BODY,{"disambiguationData":[OSD([sQuery(id+"F7.wireOp",EDGE,"E21.bottom"),sQuery(id+"F7.wireOp",EDGE,"E21.top"),sQuery(id+"F7.wireOp",EDGE,"E21.left"),sQuery(id+"F7.wireOp",EDGE,"E21.right"),sQuery(id+"F7.wireOp",EDGE,"E22.filletArc"),sQuery(id+"F7.wireOp",EDGE,"E23.filletArc"),sQuery(id+"F7.wireOp",EDGE,"E24.filletArc"),sQuery(id+"F7.wireOp",EDGE,"E25.filletArc")])]});
            hole(context, id + "F9", {"style" : HoleStyle.SIMPLE, "endStyle" : HoleEndStyle.THROUGH, "oppositeDirection" : true, "holeDiameter" : 3 * mm, "majorDiameter" : 5 * mm, "isTappedThrough" : true, "tappedDepth" : 12 * mm, "tapClearance" : 3, "locations" : qUnion([Q0, Q1, Q2, Q3]), "scope" : qUnion([Q4])});
        }
        {
            var Q0;
            Q0=makeQuery(id+"F8.opExtrude","CAP_FACE",FACE,{"disambiguationData":[OSD([sQuery(id+"F7.wireOp",EDGE,"E21.bottom"),sQuery(id+"F7.wireOp",EDGE,"E21.top"),sQuery(id+"F7.wireOp",EDGE,"E21.left"),sQuery(id+"F7.wireOp",EDGE,"E21.right"),sQuery(id+"F7.wireOp",EDGE,"E22.filletArc"),sQuery(id+"F7.wireOp",EDGE,"E23.filletArc"),sQuery(id+"F7.wireOp",EDGE,"E24.filletArc"),sQuery(id+"F7.wireOp",EDGE,"E25.filletArc")])],"isStart":true});
            shell(context, id + "F10", {"entities" : qUnion([Q0]), "thickness" : 3 * mm});
        }
    });
